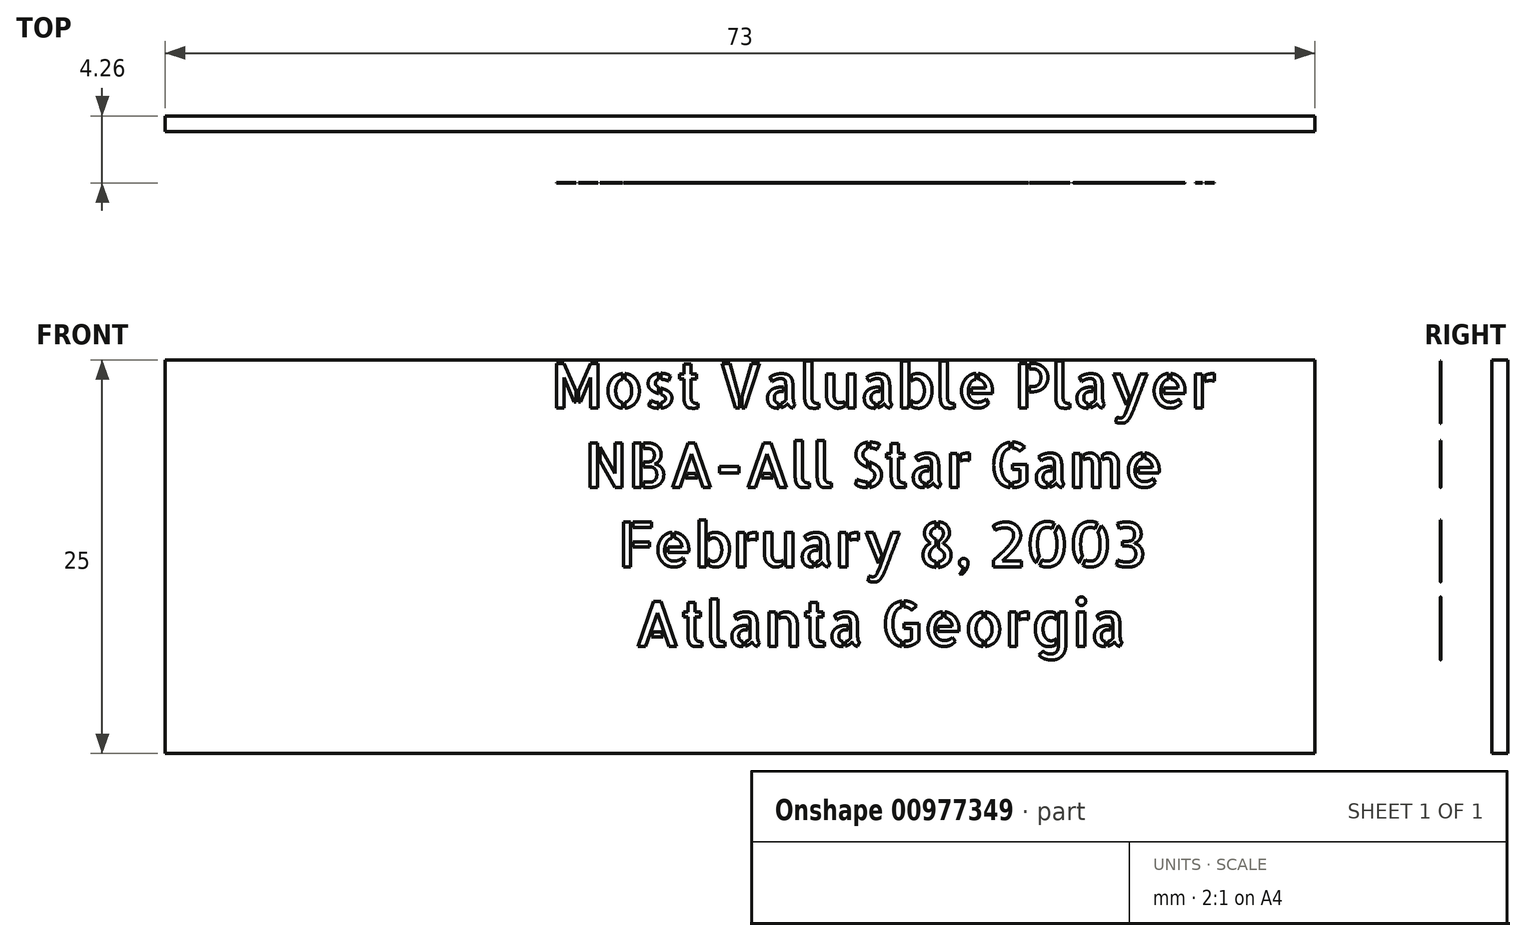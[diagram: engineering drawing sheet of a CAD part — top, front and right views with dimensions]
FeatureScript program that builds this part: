
annotation { "Feature Type Name" : "Feature", "Feature Type Description" : "" }
export const myFeature = defineFeature(function(context is Context, id is Id, definition is map)
    precondition{}
    {
        {
            var Q0;
            Q0=qCreatedBy(makeId("Front.planeOp"),FACE);
            var sketch = newSketch(context, id + "F0", { "sketchPlane" : qUnion([Q0])});
            skLineSegment(sketch, "E0.bottom", {"start": v(36.5, 12.5) * mm, "end": v(-36.5, 12.5) * mm});
            skLineSegment(sketch, "E0.top", {"start": v(36.5, -12.5) * mm, "end": v(-36.5, -12.5) * mm});
            skLineSegment(sketch, "E0.left", {"start": v(36.5, 12.5) * mm, "end": v(36.5, -12.5) * mm});
            skLineSegment(sketch, "E0.right", {"start": v(-36.5, 12.5) * mm, "end": v(-36.5, -12.5) * mm});
            skPoint(sketch, "E0.middle", {"position": v(0, 0) * mm});
            skSolve(sketch);
        }
        {
            var Q0;
            Q0 = qSketchRegion(id + "F0", true);
            extrude(context, id + "F1", {"entities" : qUnion([Q0]), "depth" : 1 * mm, "offsetDistance" : 25 * mm});
        }
        {
            var Q0;
            Q0=makeQuery(id+"F1.opExtrude","CAP_FACE",FACE,{"disambiguationData":[OSD([sQuery(id+"F0.wireOp",EDGE,"E0.bottom"),sQuery(id+"F0.wireOp",EDGE,"E0.top"),sQuery(id+"F0.wireOp",EDGE,"E0.left"),sQuery(id+"F0.wireOp",EDGE,"E0.right")])],"isStart":false});
            cPlane(context, id + "F2", {"entities" : qUnion([Q0]), "cplaneType" : CPlaneType.OFFSET, "offset" : 25 * mm, "width" : 150 * mm, "height" : 150 * mm});
        }
        {
            var Q0;
            Q0=qCreatedBy(id+"F2.planeOp",FACE);
            var sketch = newSketch(context, id + "F3", { "sketchPlane" : qUnion([Q0])});
            skText(sketch, "E1", { "text": "                       Most Valuable Player\n                         NBA-All Star Game\n                           February 8, 2003\n                            Atlanta Georgia", "fontName": "AllertaStencil-Regular.ttf"});
            const initialGuessF3  = {"E1": [-0.03462, -0.01092, 1, 0, 0.02183]};
            skSetInitialGuess(sketch, initialGuessF3);
            skSolve(sketch);
        }
        {
            var Q0;
            Q0 = qSketchRegion(id + "F3", true);
            extrude(context, id + "F4", {"entities" : qUnion([Q0]), "depth" : .1 * mm, "offsetDistance" : 25 * mm});
        }
        {
            var Q0;
            Q0=makeQuery(id+"F4.opExtrude","SWEPT_BODY",BODY,{"disambiguationData":[OSD([sQuery(id+"F3.wireOp",EDGE,"E1.sketch_text.stroke-8"),sQuery(id+"F3.wireOp",EDGE,"E1.sketch_text.stroke-9"),sQuery(id+"F3.wireOp",EDGE,"E1.sketch_text.stroke-10"),sQuery(id+"F3.wireOp",EDGE,"E1.sketch_text.stroke-11"),sQuery(id+"F3.wireOp",EDGE,"E1.sketch_text.stroke-12"),sQuery(id+"F3.wireOp",EDGE,"E1.sketch_text.stroke-13"),sQuery(id+"F3.wireOp",EDGE,"E1.sketch_text.stroke-14"),sQuery(id+"F3.wireOp",EDGE,"E1.sketch_text.stroke-15")])]});
            var Q1;
            Q1=makeQuery(id+"F4.opExtrude","SWEPT_BODY",BODY,{"disambiguationData":[OSD([sQuery(id+"F3.wireOp",EDGE,"E1.sketch_text.stroke-16"),sQuery(id+"F3.wireOp",EDGE,"E1.sketch_text.stroke-17"),sQuery(id+"F3.wireOp",EDGE,"E1.sketch_text.stroke-18"),sQuery(id+"F3.wireOp",EDGE,"E1.sketch_text.stroke-19"),sQuery(id+"F3.wireOp",EDGE,"E1.sketch_text.stroke-20"),sQuery(id+"F3.wireOp",EDGE,"E1.sketch_text.stroke-21"),sQuery(id+"F3.wireOp",EDGE,"E1.sketch_text.stroke-22"),sQuery(id+"F3.wireOp",EDGE,"E1.sketch_text.stroke-23"),sQuery(id+"F3.wireOp",EDGE,"E1.sketch_text.stroke-24"),sQuery(id+"F3.wireOp",EDGE,"E1.sketch_text.stroke-25"),sQuery(id+"F3.wireOp",EDGE,"E1.sketch_text.stroke-26"),sQuery(id+"F3.wireOp",EDGE,"E1.sketch_text.stroke-27"),sQuery(id+"F3.wireOp",EDGE,"E1.sketch_text.stroke-28"),sQuery(id+"F3.wireOp",EDGE,"E1.sketch_text.stroke-29"),sQuery(id+"F3.wireOp",EDGE,"E1.sketch_text.stroke-30"),sQuery(id+"F3.wireOp",EDGE,"E1.sketch_text.stroke-31")])]});
            var Q2;
            Q2=makeQuery(id+"F4.opExtrude","SWEPT_BODY",BODY,{"disambiguationData":[OSD([sQuery(id+"F3.wireOp",EDGE,"E1.sketch_text.stroke-32"),sQuery(id+"F3.wireOp",EDGE,"E1.sketch_text.stroke-33"),sQuery(id+"F3.wireOp",EDGE,"E1.sketch_text.stroke-34"),sQuery(id+"F3.wireOp",EDGE,"E1.sketch_text.stroke-35"),sQuery(id+"F3.wireOp",EDGE,"E1.sketch_text.stroke-36"),sQuery(id+"F3.wireOp",EDGE,"E1.sketch_text.stroke-37"),sQuery(id+"F3.wireOp",EDGE,"E1.sketch_text.stroke-38"),sQuery(id+"F3.wireOp",EDGE,"E1.sketch_text.stroke-39"),sQuery(id+"F3.wireOp",EDGE,"E1.sketch_text.stroke-40"),sQuery(id+"F3.wireOp",EDGE,"E1.sketch_text.stroke-41"),sQuery(id+"F3.wireOp",EDGE,"E1.sketch_text.stroke-42"),sQuery(id+"F3.wireOp",EDGE,"E1.sketch_text.stroke-43"),sQuery(id+"F3.wireOp",EDGE,"E1.sketch_text.stroke-44"),sQuery(id+"F3.wireOp",EDGE,"E1.sketch_text.stroke-45"),sQuery(id+"F3.wireOp",EDGE,"E1.sketch_text.stroke-46"),sQuery(id+"F3.wireOp",EDGE,"E1.sketch_text.stroke-47")])]});
            var Q3;
            Q3=makeQuery(id+"F4.opExtrude","SWEPT_BODY",BODY,{"disambiguationData":[OSD([sQuery(id+"F3.wireOp",EDGE,"E1.sketch_text.stroke-48"),sQuery(id+"F3.wireOp",EDGE,"E1.sketch_text.stroke-49"),sQuery(id+"F3.wireOp",EDGE,"E1.sketch_text.stroke-50"),sQuery(id+"F3.wireOp",EDGE,"E1.sketch_text.stroke-51"),sQuery(id+"F3.wireOp",EDGE,"E1.sketch_text.stroke-52"),sQuery(id+"F3.wireOp",EDGE,"E1.sketch_text.stroke-53"),sQuery(id+"F3.wireOp",EDGE,"E1.sketch_text.stroke-54"),sQuery(id+"F3.wireOp",EDGE,"E1.sketch_text.stroke-55"),sQuery(id+"F3.wireOp",EDGE,"E1.sketch_text.stroke-56"),sQuery(id+"F3.wireOp",EDGE,"E1.sketch_text.stroke-57"),sQuery(id+"F3.wireOp",EDGE,"E1.sketch_text.stroke-58"),sQuery(id+"F3.wireOp",EDGE,"E1.sketch_text.stroke-59"),sQuery(id+"F3.wireOp",EDGE,"E1.sketch_text.stroke-60"),sQuery(id+"F3.wireOp",EDGE,"E1.sketch_text.stroke-61")])]});
            var Q4;
            Q4=makeQuery(id+"F4.opExtrude","SWEPT_BODY",BODY,{"disambiguationData":[OSD([sQuery(id+"F3.wireOp",EDGE,"E1.sketch_text.stroke-62"),sQuery(id+"F3.wireOp",EDGE,"E1.sketch_text.stroke-63"),sQuery(id+"F3.wireOp",EDGE,"E1.sketch_text.stroke-64"),sQuery(id+"F3.wireOp",EDGE,"E1.sketch_text.stroke-65"),sQuery(id+"F3.wireOp",EDGE,"E1.sketch_text.stroke-66"),sQuery(id+"F3.wireOp",EDGE,"E1.sketch_text.stroke-67")])]});
            var Q5;
            Q5=makeQuery(id+"F4.opExtrude","SWEPT_BODY",BODY,{"disambiguationData":[OSD([sQuery(id+"F3.wireOp",EDGE,"E1.sketch_text.stroke-68"),sQuery(id+"F3.wireOp",EDGE,"E1.sketch_text.stroke-69"),sQuery(id+"F3.wireOp",EDGE,"E1.sketch_text.stroke-70"),sQuery(id+"F3.wireOp",EDGE,"E1.sketch_text.stroke-71"),sQuery(id+"F3.wireOp",EDGE,"E1.sketch_text.stroke-72"),sQuery(id+"F3.wireOp",EDGE,"E1.sketch_text.stroke-73"),sQuery(id+"F3.wireOp",EDGE,"E1.sketch_text.stroke-74"),sQuery(id+"F3.wireOp",EDGE,"E1.sketch_text.stroke-75"),sQuery(id+"F3.wireOp",EDGE,"E1.sketch_text.stroke-76")])]});
            var Q6;
            Q6=makeQuery(id+"F4.opExtrude","SWEPT_BODY",BODY,{"disambiguationData":[OSD([sQuery(id+"F3.wireOp",EDGE,"E1.sketch_text.stroke-77"),sQuery(id+"F3.wireOp",EDGE,"E1.sketch_text.stroke-78"),sQuery(id+"F3.wireOp",EDGE,"E1.sketch_text.stroke-79"),sQuery(id+"F3.wireOp",EDGE,"E1.sketch_text.stroke-80"),sQuery(id+"F3.wireOp",EDGE,"E1.sketch_text.stroke-81"),sQuery(id+"F3.wireOp",EDGE,"E1.sketch_text.stroke-82"),sQuery(id+"F3.wireOp",EDGE,"E1.sketch_text.stroke-83"),sQuery(id+"F3.wireOp",EDGE,"E1.sketch_text.stroke-84"),sQuery(id+"F3.wireOp",EDGE,"E1.sketch_text.stroke-85"),sQuery(id+"F3.wireOp",EDGE,"E1.sketch_text.stroke-86"),sQuery(id+"F3.wireOp",EDGE,"E1.sketch_text.stroke-87"),sQuery(id+"F3.wireOp",EDGE,"E1.sketch_text.stroke-88"),sQuery(id+"F3.wireOp",EDGE,"E1.sketch_text.stroke-89"),sQuery(id+"F3.wireOp",EDGE,"E1.sketch_text.stroke-90")])]});
            var Q7;
            Q7=makeQuery(id+"F4.opExtrude","SWEPT_BODY",BODY,{"disambiguationData":[OSD([sQuery(id+"F3.wireOp",EDGE,"E1.sketch_text.stroke-91"),sQuery(id+"F3.wireOp",EDGE,"E1.sketch_text.stroke-92"),sQuery(id+"F3.wireOp",EDGE,"E1.sketch_text.stroke-93"),sQuery(id+"F3.wireOp",EDGE,"E1.sketch_text.stroke-94"),sQuery(id+"F3.wireOp",EDGE,"E1.sketch_text.stroke-95"),sQuery(id+"F3.wireOp",EDGE,"E1.sketch_text.stroke-96"),sQuery(id+"F3.wireOp",EDGE,"E1.sketch_text.stroke-97"),sQuery(id+"F3.wireOp",EDGE,"E1.sketch_text.stroke-98"),sQuery(id+"F3.wireOp",EDGE,"E1.sketch_text.stroke-99"),sQuery(id+"F3.wireOp",EDGE,"E1.sketch_text.stroke-100"),sQuery(id+"F3.wireOp",EDGE,"E1.sketch_text.stroke-101"),sQuery(id+"F3.wireOp",EDGE,"E1.sketch_text.stroke-102"),sQuery(id+"F3.wireOp",EDGE,"E1.sketch_text.stroke-103"),sQuery(id+"F3.wireOp",EDGE,"E1.sketch_text.stroke-104"),sQuery(id+"F3.wireOp",EDGE,"E1.sketch_text.stroke-105"),sQuery(id+"F3.wireOp",EDGE,"E1.sketch_text.stroke-106"),sQuery(id+"F3.wireOp",EDGE,"E1.sketch_text.stroke-107"),sQuery(id+"F3.wireOp",EDGE,"E1.sketch_text.stroke-108"),sQuery(id+"F3.wireOp",EDGE,"E1.sketch_text.stroke-109"),sQuery(id+"F3.wireOp",EDGE,"E1.sketch_text.stroke-110"),sQuery(id+"F3.wireOp",EDGE,"E1.sketch_text.stroke-111"),sQuery(id+"F3.wireOp",EDGE,"E1.sketch_text.stroke-112"),sQuery(id+"F3.wireOp",EDGE,"E1.sketch_text.stroke-113"),sQuery(id+"F3.wireOp",EDGE,"E1.sketch_text.stroke-114"),sQuery(id+"F3.wireOp",EDGE,"E1.sketch_text.stroke-115")])]});
            var Q8;
            Q8=makeQuery(id+"F4.opExtrude","SWEPT_BODY",BODY,{"disambiguationData":[OSD([sQuery(id+"F3.wireOp",EDGE,"E1.sketch_text.stroke-116"),sQuery(id+"F3.wireOp",EDGE,"E1.sketch_text.stroke-117"),sQuery(id+"F3.wireOp",EDGE,"E1.sketch_text.stroke-118"),sQuery(id+"F3.wireOp",EDGE,"E1.sketch_text.stroke-119"),sQuery(id+"F3.wireOp",EDGE,"E1.sketch_text.stroke-120")])]});
            var Q9;
            Q9=makeQuery(id+"F4.opExtrude","SWEPT_BODY",BODY,{"disambiguationData":[OSD([sQuery(id+"F3.wireOp",EDGE,"E1.sketch_text.stroke-121"),sQuery(id+"F3.wireOp",EDGE,"E1.sketch_text.stroke-122"),sQuery(id+"F3.wireOp",EDGE,"E1.sketch_text.stroke-123"),sQuery(id+"F3.wireOp",EDGE,"E1.sketch_text.stroke-124"),sQuery(id+"F3.wireOp",EDGE,"E1.sketch_text.stroke-125")])]});
            var Q10;
            Q10=makeQuery(id+"F4.opExtrude","SWEPT_BODY",BODY,{"disambiguationData":[OSD([sQuery(id+"F3.wireOp",EDGE,"E1.sketch_text.stroke-126"),sQuery(id+"F3.wireOp",EDGE,"E1.sketch_text.stroke-127"),sQuery(id+"F3.wireOp",EDGE,"E1.sketch_text.stroke-128"),sQuery(id+"F3.wireOp",EDGE,"E1.sketch_text.stroke-129"),sQuery(id+"F3.wireOp",EDGE,"E1.sketch_text.stroke-130"),sQuery(id+"F3.wireOp",EDGE,"E1.sketch_text.stroke-131"),sQuery(id+"F3.wireOp",EDGE,"E1.sketch_text.stroke-132"),sQuery(id+"F3.wireOp",EDGE,"E1.sketch_text.stroke-133"),sQuery(id+"F3.wireOp",EDGE,"E1.sketch_text.stroke-134"),sQuery(id+"F3.wireOp",EDGE,"E1.sketch_text.stroke-135"),sQuery(id+"F3.wireOp",EDGE,"E1.sketch_text.stroke-136"),sQuery(id+"F3.wireOp",EDGE,"E1.sketch_text.stroke-137"),sQuery(id+"F3.wireOp",EDGE,"E1.sketch_text.stroke-138"),sQuery(id+"F3.wireOp",EDGE,"E1.sketch_text.stroke-139"),sQuery(id+"F3.wireOp",EDGE,"E1.sketch_text.stroke-140"),sQuery(id+"F3.wireOp",EDGE,"E1.sketch_text.stroke-141"),sQuery(id+"F3.wireOp",EDGE,"E1.sketch_text.stroke-142"),sQuery(id+"F3.wireOp",EDGE,"E1.sketch_text.stroke-143"),sQuery(id+"F3.wireOp",EDGE,"E1.sketch_text.stroke-144")])]});
            var Q11;
            Q11=makeQuery(id+"F4.opExtrude","SWEPT_BODY",BODY,{"disambiguationData":[OSD([sQuery(id+"F3.wireOp",EDGE,"E1.sketch_text.stroke-145"),sQuery(id+"F3.wireOp",EDGE,"E1.sketch_text.stroke-146"),sQuery(id+"F3.wireOp",EDGE,"E1.sketch_text.stroke-147"),sQuery(id+"F3.wireOp",EDGE,"E1.sketch_text.stroke-148"),sQuery(id+"F3.wireOp",EDGE,"E1.sketch_text.stroke-149"),sQuery(id+"F3.wireOp",EDGE,"E1.sketch_text.stroke-150"),sQuery(id+"F3.wireOp",EDGE,"E1.sketch_text.stroke-151"),sQuery(id+"F3.wireOp",EDGE,"E1.sketch_text.stroke-152"),sQuery(id+"F3.wireOp",EDGE,"E1.sketch_text.stroke-153"),sQuery(id+"F3.wireOp",EDGE,"E1.sketch_text.stroke-154"),sQuery(id+"F3.wireOp",EDGE,"E1.sketch_text.stroke-155"),sQuery(id+"F3.wireOp",EDGE,"E1.sketch_text.stroke-156"),sQuery(id+"F3.wireOp",EDGE,"E1.sketch_text.stroke-157"),sQuery(id+"F3.wireOp",EDGE,"E1.sketch_text.stroke-158"),sQuery(id+"F3.wireOp",EDGE,"E1.sketch_text.stroke-159"),sQuery(id+"F3.wireOp",EDGE,"E1.sketch_text.stroke-160"),sQuery(id+"F3.wireOp",EDGE,"E1.sketch_text.stroke-161"),sQuery(id+"F3.wireOp",EDGE,"E1.sketch_text.stroke-162"),sQuery(id+"F3.wireOp",EDGE,"E1.sketch_text.stroke-163"),sQuery(id+"F3.wireOp",EDGE,"E1.sketch_text.stroke-164"),sQuery(id+"F3.wireOp",EDGE,"E1.sketch_text.stroke-165"),sQuery(id+"F3.wireOp",EDGE,"E1.sketch_text.stroke-166"),sQuery(id+"F3.wireOp",EDGE,"E1.sketch_text.stroke-167"),sQuery(id+"F3.wireOp",EDGE,"E1.sketch_text.stroke-168"),sQuery(id+"F3.wireOp",EDGE,"E1.sketch_text.stroke-169"),sQuery(id+"F3.wireOp",EDGE,"E1.sketch_text.stroke-170"),sQuery(id+"F3.wireOp",EDGE,"E1.sketch_text.stroke-171"),sQuery(id+"F3.wireOp",EDGE,"E1.sketch_text.stroke-172"),sQuery(id+"F3.wireOp",EDGE,"E1.sketch_text.stroke-173"),sQuery(id+"F3.wireOp",EDGE,"E1.sketch_text.stroke-174"),sQuery(id+"F3.wireOp",EDGE,"E1.sketch_text.stroke-175"),sQuery(id+"F3.wireOp",EDGE,"E1.sketch_text.stroke-176"),sQuery(id+"F3.wireOp",EDGE,"E1.sketch_text.stroke-177"),sQuery(id+"F3.wireOp",EDGE,"E1.sketch_text.stroke-178"),sQuery(id+"F3.wireOp",EDGE,"E1.sketch_text.stroke-179"),sQuery(id+"F3.wireOp",EDGE,"E1.sketch_text.stroke-180")])]});
            var Q12;
            Q12=makeQuery(id+"F4.opExtrude","SWEPT_BODY",BODY,{"disambiguationData":[OSD([sQuery(id+"F3.wireOp",EDGE,"E1.sketch_text.stroke-181"),sQuery(id+"F3.wireOp",EDGE,"E1.sketch_text.stroke-182"),sQuery(id+"F3.wireOp",EDGE,"E1.sketch_text.stroke-183"),sQuery(id+"F3.wireOp",EDGE,"E1.sketch_text.stroke-184"),sQuery(id+"F3.wireOp",EDGE,"E1.sketch_text.stroke-185"),sQuery(id+"F3.wireOp",EDGE,"E1.sketch_text.stroke-186"),sQuery(id+"F3.wireOp",EDGE,"E1.sketch_text.stroke-187"),sQuery(id+"F3.wireOp",EDGE,"E1.sketch_text.stroke-188"),sQuery(id+"F3.wireOp",EDGE,"E1.sketch_text.stroke-189"),sQuery(id+"F3.wireOp",EDGE,"E1.sketch_text.stroke-190"),sQuery(id+"F3.wireOp",EDGE,"E1.sketch_text.stroke-191"),sQuery(id+"F3.wireOp",EDGE,"E1.sketch_text.stroke-192"),sQuery(id+"F3.wireOp",EDGE,"E1.sketch_text.stroke-193"),sQuery(id+"F3.wireOp",EDGE,"E1.sketch_text.stroke-194"),sQuery(id+"F3.wireOp",EDGE,"E1.sketch_text.stroke-195"),sQuery(id+"F3.wireOp",EDGE,"E1.sketch_text.stroke-196"),sQuery(id+"F3.wireOp",EDGE,"E1.sketch_text.stroke-197"),sQuery(id+"F3.wireOp",EDGE,"E1.sketch_text.stroke-198")])]});
            var Q13;
            Q13=makeQuery(id+"F4.opExtrude","SWEPT_BODY",BODY,{"disambiguationData":[OSD([sQuery(id+"F3.wireOp",EDGE,"E1.sketch_text.stroke-199"),sQuery(id+"F3.wireOp",EDGE,"E1.sketch_text.stroke-200"),sQuery(id+"F3.wireOp",EDGE,"E1.sketch_text.stroke-201"),sQuery(id+"F3.wireOp",EDGE,"E1.sketch_text.stroke-202"),sQuery(id+"F3.wireOp",EDGE,"E1.sketch_text.stroke-203"),sQuery(id+"F3.wireOp",EDGE,"E1.sketch_text.stroke-204"),sQuery(id+"F3.wireOp",EDGE,"E1.sketch_text.stroke-205"),sQuery(id+"F3.wireOp",EDGE,"E1.sketch_text.stroke-206"),sQuery(id+"F3.wireOp",EDGE,"E1.sketch_text.stroke-207"),sQuery(id+"F3.wireOp",EDGE,"E1.sketch_text.stroke-208"),sQuery(id+"F3.wireOp",EDGE,"E1.sketch_text.stroke-209"),sQuery(id+"F3.wireOp",EDGE,"E1.sketch_text.stroke-210"),sQuery(id+"F3.wireOp",EDGE,"E1.sketch_text.stroke-211"),sQuery(id+"F3.wireOp",EDGE,"E1.sketch_text.stroke-212"),sQuery(id+"F3.wireOp",EDGE,"E1.sketch_text.stroke-213"),sQuery(id+"F3.wireOp",EDGE,"E1.sketch_text.stroke-214"),sQuery(id+"F3.wireOp",EDGE,"E1.sketch_text.stroke-215"),sQuery(id+"F3.wireOp",EDGE,"E1.sketch_text.stroke-216"),sQuery(id+"F3.wireOp",EDGE,"E1.sketch_text.stroke-217"),sQuery(id+"F3.wireOp",EDGE,"E1.sketch_text.stroke-218")])]});
            var Q14;
            Q14=makeQuery(id+"F4.opExtrude","SWEPT_BODY",BODY,{"disambiguationData":[OSD([sQuery(id+"F3.wireOp",EDGE,"E1.sketch_text.stroke-219"),sQuery(id+"F3.wireOp",EDGE,"E1.sketch_text.stroke-220"),sQuery(id+"F3.wireOp",EDGE,"E1.sketch_text.stroke-221"),sQuery(id+"F3.wireOp",EDGE,"E1.sketch_text.stroke-222"),sQuery(id+"F3.wireOp",EDGE,"E1.sketch_text.stroke-223")])]});
            var Q15;
            Q15=makeQuery(id+"F4.opExtrude","SWEPT_BODY",BODY,{"disambiguationData":[OSD([sQuery(id+"F3.wireOp",EDGE,"E1.sketch_text.stroke-224"),sQuery(id+"F3.wireOp",EDGE,"E1.sketch_text.stroke-225"),sQuery(id+"F3.wireOp",EDGE,"E1.sketch_text.stroke-226"),sQuery(id+"F3.wireOp",EDGE,"E1.sketch_text.stroke-227"),sQuery(id+"F3.wireOp",EDGE,"E1.sketch_text.stroke-228"),sQuery(id+"F3.wireOp",EDGE,"E1.sketch_text.stroke-229"),sQuery(id+"F3.wireOp",EDGE,"E1.sketch_text.stroke-230"),sQuery(id+"F3.wireOp",EDGE,"E1.sketch_text.stroke-231"),sQuery(id+"F3.wireOp",EDGE,"E1.sketch_text.stroke-232"),sQuery(id+"F3.wireOp",EDGE,"E1.sketch_text.stroke-233"),sQuery(id+"F3.wireOp",EDGE,"E1.sketch_text.stroke-234"),sQuery(id+"F3.wireOp",EDGE,"E1.sketch_text.stroke-235"),sQuery(id+"F3.wireOp",EDGE,"E1.sketch_text.stroke-236"),sQuery(id+"F3.wireOp",EDGE,"E1.sketch_text.stroke-237"),sQuery(id+"F3.wireOp",EDGE,"E1.sketch_text.stroke-238"),sQuery(id+"F3.wireOp",EDGE,"E1.sketch_text.stroke-239"),sQuery(id+"F3.wireOp",EDGE,"E1.sketch_text.stroke-240"),sQuery(id+"F3.wireOp",EDGE,"E1.sketch_text.stroke-241"),sQuery(id+"F3.wireOp",EDGE,"E1.sketch_text.stroke-242")])]});
            var Q16;
            Q16=makeQuery(id+"F4.opExtrude","SWEPT_BODY",BODY,{"disambiguationData":[OSD([sQuery(id+"F3.wireOp",EDGE,"E1.sketch_text.stroke-243"),sQuery(id+"F3.wireOp",EDGE,"E1.sketch_text.stroke-244"),sQuery(id+"F3.wireOp",EDGE,"E1.sketch_text.stroke-245"),sQuery(id+"F3.wireOp",EDGE,"E1.sketch_text.stroke-246"),sQuery(id+"F3.wireOp",EDGE,"E1.sketch_text.stroke-247"),sQuery(id+"F3.wireOp",EDGE,"E1.sketch_text.stroke-248"),sQuery(id+"F3.wireOp",EDGE,"E1.sketch_text.stroke-249"),sQuery(id+"F3.wireOp",EDGE,"E1.sketch_text.stroke-250"),sQuery(id+"F3.wireOp",EDGE,"E1.sketch_text.stroke-251"),sQuery(id+"F3.wireOp",EDGE,"E1.sketch_text.stroke-252"),sQuery(id+"F3.wireOp",EDGE,"E1.sketch_text.stroke-253"),sQuery(id+"F3.wireOp",EDGE,"E1.sketch_text.stroke-254"),sQuery(id+"F3.wireOp",EDGE,"E1.sketch_text.stroke-255"),sQuery(id+"F3.wireOp",EDGE,"E1.sketch_text.stroke-256"),sQuery(id+"F3.wireOp",EDGE,"E1.sketch_text.stroke-257"),sQuery(id+"F3.wireOp",EDGE,"E1.sketch_text.stroke-258"),sQuery(id+"F3.wireOp",EDGE,"E1.sketch_text.stroke-259"),sQuery(id+"F3.wireOp",EDGE,"E1.sketch_text.stroke-260"),sQuery(id+"F3.wireOp",EDGE,"E1.sketch_text.stroke-261"),sQuery(id+"F3.wireOp",EDGE,"E1.sketch_text.stroke-262"),sQuery(id+"F3.wireOp",EDGE,"E1.sketch_text.stroke-263"),sQuery(id+"F3.wireOp",EDGE,"E1.sketch_text.stroke-264"),sQuery(id+"F3.wireOp",EDGE,"E1.sketch_text.stroke-265"),sQuery(id+"F3.wireOp",EDGE,"E1.sketch_text.stroke-266"),sQuery(id+"F3.wireOp",EDGE,"E1.sketch_text.stroke-267"),sQuery(id+"F3.wireOp",EDGE,"E1.sketch_text.stroke-268"),sQuery(id+"F3.wireOp",EDGE,"E1.sketch_text.stroke-269"),sQuery(id+"F3.wireOp",EDGE,"E1.sketch_text.stroke-270"),sQuery(id+"F3.wireOp",EDGE,"E1.sketch_text.stroke-271"),sQuery(id+"F3.wireOp",EDGE,"E1.sketch_text.stroke-272"),sQuery(id+"F3.wireOp",EDGE,"E1.sketch_text.stroke-273"),sQuery(id+"F3.wireOp",EDGE,"E1.sketch_text.stroke-274"),sQuery(id+"F3.wireOp",EDGE,"E1.sketch_text.stroke-275"),sQuery(id+"F3.wireOp",EDGE,"E1.sketch_text.stroke-276"),sQuery(id+"F3.wireOp",EDGE,"E1.sketch_text.stroke-277"),sQuery(id+"F3.wireOp",EDGE,"E1.sketch_text.stroke-278")])]});
            var Q17;
            Q17=makeQuery(id+"F4.opExtrude","SWEPT_BODY",BODY,{"disambiguationData":[OSD([sQuery(id+"F3.wireOp",EDGE,"E1.sketch_text.stroke-279"),sQuery(id+"F3.wireOp",EDGE,"E1.sketch_text.stroke-280"),sQuery(id+"F3.wireOp",EDGE,"E1.sketch_text.stroke-281"),sQuery(id+"F3.wireOp",EDGE,"E1.sketch_text.stroke-282"),sQuery(id+"F3.wireOp",EDGE,"E1.sketch_text.stroke-283"),sQuery(id+"F3.wireOp",EDGE,"E1.sketch_text.stroke-284")])]});
            var Q18;
            Q18=makeQuery(id+"F4.opExtrude","SWEPT_BODY",BODY,{"disambiguationData":[OSD([sQuery(id+"F3.wireOp",EDGE,"E1.sketch_text.stroke-285"),sQuery(id+"F3.wireOp",EDGE,"E1.sketch_text.stroke-286"),sQuery(id+"F3.wireOp",EDGE,"E1.sketch_text.stroke-287"),sQuery(id+"F3.wireOp",EDGE,"E1.sketch_text.stroke-288"),sQuery(id+"F3.wireOp",EDGE,"E1.sketch_text.stroke-289"),sQuery(id+"F3.wireOp",EDGE,"E1.sketch_text.stroke-290"),sQuery(id+"F3.wireOp",EDGE,"E1.sketch_text.stroke-291"),sQuery(id+"F3.wireOp",EDGE,"E1.sketch_text.stroke-292"),sQuery(id+"F3.wireOp",EDGE,"E1.sketch_text.stroke-293"),sQuery(id+"F3.wireOp",EDGE,"E1.sketch_text.stroke-294"),sQuery(id+"F3.wireOp",EDGE,"E1.sketch_text.stroke-295"),sQuery(id+"F3.wireOp",EDGE,"E1.sketch_text.stroke-296"),sQuery(id+"F3.wireOp",EDGE,"E1.sketch_text.stroke-297"),sQuery(id+"F3.wireOp",EDGE,"E1.sketch_text.stroke-298"),sQuery(id+"F3.wireOp",EDGE,"E1.sketch_text.stroke-299"),sQuery(id+"F3.wireOp",EDGE,"E1.sketch_text.stroke-300"),sQuery(id+"F3.wireOp",EDGE,"E1.sketch_text.stroke-301"),sQuery(id+"F3.wireOp",EDGE,"E1.sketch_text.stroke-302"),sQuery(id+"F3.wireOp",EDGE,"E1.sketch_text.stroke-303"),sQuery(id+"F3.wireOp",EDGE,"E1.sketch_text.stroke-304"),sQuery(id+"F3.wireOp",EDGE,"E1.sketch_text.stroke-305"),sQuery(id+"F3.wireOp",EDGE,"E1.sketch_text.stroke-306"),sQuery(id+"F3.wireOp",EDGE,"E1.sketch_text.stroke-307"),sQuery(id+"F3.wireOp",EDGE,"E1.sketch_text.stroke-308"),sQuery(id+"F3.wireOp",EDGE,"E1.sketch_text.stroke-309"),sQuery(id+"F3.wireOp",EDGE,"E1.sketch_text.stroke-310"),sQuery(id+"F3.wireOp",EDGE,"E1.sketch_text.stroke-311")])]});
            var Q19;
            Q19=makeQuery(id+"F4.opExtrude","SWEPT_BODY",BODY,{"disambiguationData":[OSD([sQuery(id+"F3.wireOp",EDGE,"E1.sketch_text.stroke-312"),sQuery(id+"F3.wireOp",EDGE,"E1.sketch_text.stroke-313"),sQuery(id+"F3.wireOp",EDGE,"E1.sketch_text.stroke-314"),sQuery(id+"F3.wireOp",EDGE,"E1.sketch_text.stroke-315"),sQuery(id+"F3.wireOp",EDGE,"E1.sketch_text.stroke-316"),sQuery(id+"F3.wireOp",EDGE,"E1.sketch_text.stroke-317"),sQuery(id+"F3.wireOp",EDGE,"E1.sketch_text.stroke-318"),sQuery(id+"F3.wireOp",EDGE,"E1.sketch_text.stroke-319"),sQuery(id+"F3.wireOp",EDGE,"E1.sketch_text.stroke-320"),sQuery(id+"F3.wireOp",EDGE,"E1.sketch_text.stroke-321"),sQuery(id+"F3.wireOp",EDGE,"E1.sketch_text.stroke-322"),sQuery(id+"F3.wireOp",EDGE,"E1.sketch_text.stroke-323"),sQuery(id+"F3.wireOp",EDGE,"E1.sketch_text.stroke-324"),sQuery(id+"F3.wireOp",EDGE,"E1.sketch_text.stroke-325"),sQuery(id+"F3.wireOp",EDGE,"E1.sketch_text.stroke-326"),sQuery(id+"F3.wireOp",EDGE,"E1.sketch_text.stroke-327"),sQuery(id+"F3.wireOp",EDGE,"E1.sketch_text.stroke-328"),sQuery(id+"F3.wireOp",EDGE,"E1.sketch_text.stroke-329")])]});
            var Q20;
            Q20=makeQuery(id+"F4.opExtrude","SWEPT_BODY",BODY,{"disambiguationData":[OSD([sQuery(id+"F3.wireOp",EDGE,"E1.sketch_text.stroke-330"),sQuery(id+"F3.wireOp",EDGE,"E1.sketch_text.stroke-331"),sQuery(id+"F3.wireOp",EDGE,"E1.sketch_text.stroke-332"),sQuery(id+"F3.wireOp",EDGE,"E1.sketch_text.stroke-333"),sQuery(id+"F3.wireOp",EDGE,"E1.sketch_text.stroke-334"),sQuery(id+"F3.wireOp",EDGE,"E1.sketch_text.stroke-335"),sQuery(id+"F3.wireOp",EDGE,"E1.sketch_text.stroke-336"),sQuery(id+"F3.wireOp",EDGE,"E1.sketch_text.stroke-337"),sQuery(id+"F3.wireOp",EDGE,"E1.sketch_text.stroke-338"),sQuery(id+"F3.wireOp",EDGE,"E1.sketch_text.stroke-339"),sQuery(id+"F3.wireOp",EDGE,"E1.sketch_text.stroke-340"),sQuery(id+"F3.wireOp",EDGE,"E1.sketch_text.stroke-341"),sQuery(id+"F3.wireOp",EDGE,"E1.sketch_text.stroke-342")])]});
            var Q21;
            Q21=makeQuery(id+"F4.opExtrude","SWEPT_BODY",BODY,{"disambiguationData":[OSD([sQuery(id+"F3.wireOp",EDGE,"E1.sketch_text.stroke-343"),sQuery(id+"F3.wireOp",EDGE,"E1.sketch_text.stroke-344"),sQuery(id+"F3.wireOp",EDGE,"E1.sketch_text.stroke-345"),sQuery(id+"F3.wireOp",EDGE,"E1.sketch_text.stroke-346"),sQuery(id+"F3.wireOp",EDGE,"E1.sketch_text.stroke-347"),sQuery(id+"F3.wireOp",EDGE,"E1.sketch_text.stroke-348"),sQuery(id+"F3.wireOp",EDGE,"E1.sketch_text.stroke-349"),sQuery(id+"F3.wireOp",EDGE,"E1.sketch_text.stroke-350"),sQuery(id+"F3.wireOp",EDGE,"E1.sketch_text.stroke-351"),sQuery(id+"F3.wireOp",EDGE,"E1.sketch_text.stroke-352"),sQuery(id+"F3.wireOp",EDGE,"E1.sketch_text.stroke-353"),sQuery(id+"F3.wireOp",EDGE,"E1.sketch_text.stroke-354"),sQuery(id+"F3.wireOp",EDGE,"E1.sketch_text.stroke-355"),sQuery(id+"F3.wireOp",EDGE,"E1.sketch_text.stroke-356"),sQuery(id+"F3.wireOp",EDGE,"E1.sketch_text.stroke-357"),sQuery(id+"F3.wireOp",EDGE,"E1.sketch_text.stroke-358"),sQuery(id+"F3.wireOp",EDGE,"E1.sketch_text.stroke-359"),sQuery(id+"F3.wireOp",EDGE,"E1.sketch_text.stroke-360"),sQuery(id+"F3.wireOp",EDGE,"E1.sketch_text.stroke-361"),sQuery(id+"F3.wireOp",EDGE,"E1.sketch_text.stroke-362"),sQuery(id+"F3.wireOp",EDGE,"E1.sketch_text.stroke-363"),sQuery(id+"F3.wireOp",EDGE,"E1.sketch_text.stroke-364"),sQuery(id+"F3.wireOp",EDGE,"E1.sketch_text.stroke-365"),sQuery(id+"F3.wireOp",EDGE,"E1.sketch_text.stroke-366")])]});
            var Q22;
            Q22=makeQuery(id+"F4.opExtrude","SWEPT_BODY",BODY,{"disambiguationData":[OSD([sQuery(id+"F3.wireOp",EDGE,"E1.sketch_text.stroke-367"),sQuery(id+"F3.wireOp",EDGE,"E1.sketch_text.stroke-368"),sQuery(id+"F3.wireOp",EDGE,"E1.sketch_text.stroke-369"),sQuery(id+"F3.wireOp",EDGE,"E1.sketch_text.stroke-370")])]});
            var Q23;
            Q23=makeQuery(id+"F4.opExtrude","SWEPT_BODY",BODY,{"disambiguationData":[OSD([sQuery(id+"F3.wireOp",EDGE,"E1.sketch_text.stroke-371"),sQuery(id+"F3.wireOp",EDGE,"E1.sketch_text.stroke-372"),sQuery(id+"F3.wireOp",EDGE,"E1.sketch_text.stroke-373"),sQuery(id+"F3.wireOp",EDGE,"E1.sketch_text.stroke-374"),sQuery(id+"F3.wireOp",EDGE,"E1.sketch_text.stroke-375"),sQuery(id+"F3.wireOp",EDGE,"E1.sketch_text.stroke-376"),sQuery(id+"F3.wireOp",EDGE,"E1.sketch_text.stroke-377"),sQuery(id+"F3.wireOp",EDGE,"E1.sketch_text.stroke-378"),sQuery(id+"F3.wireOp",EDGE,"E1.sketch_text.stroke-379"),sQuery(id+"F3.wireOp",EDGE,"E1.sketch_text.stroke-380"),sQuery(id+"F3.wireOp",EDGE,"E1.sketch_text.stroke-381"),sQuery(id+"F3.wireOp",EDGE,"E1.sketch_text.stroke-382"),sQuery(id+"F3.wireOp",EDGE,"E1.sketch_text.stroke-383"),sQuery(id+"F3.wireOp",EDGE,"E1.sketch_text.stroke-384"),sQuery(id+"F3.wireOp",EDGE,"E1.sketch_text.stroke-385"),sQuery(id+"F3.wireOp",EDGE,"E1.sketch_text.stroke-386"),sQuery(id+"F3.wireOp",EDGE,"E1.sketch_text.stroke-387"),sQuery(id+"F3.wireOp",EDGE,"E1.sketch_text.stroke-388"),sQuery(id+"F3.wireOp",EDGE,"E1.sketch_text.stroke-389"),sQuery(id+"F3.wireOp",EDGE,"E1.sketch_text.stroke-390"),sQuery(id+"F3.wireOp",EDGE,"E1.sketch_text.stroke-391"),sQuery(id+"F3.wireOp",EDGE,"E1.sketch_text.stroke-392")])]});
            var Q24;
            Q24=makeQuery(id+"F4.opExtrude","SWEPT_BODY",BODY,{"disambiguationData":[OSD([sQuery(id+"F3.wireOp",EDGE,"E1.sketch_text.stroke-393"),sQuery(id+"F3.wireOp",EDGE,"E1.sketch_text.stroke-394"),sQuery(id+"F3.wireOp",EDGE,"E1.sketch_text.stroke-395"),sQuery(id+"F3.wireOp",EDGE,"E1.sketch_text.stroke-396"),sQuery(id+"F3.wireOp",EDGE,"E1.sketch_text.stroke-397"),sQuery(id+"F3.wireOp",EDGE,"E1.sketch_text.stroke-398"),sQuery(id+"F3.wireOp",EDGE,"E1.sketch_text.stroke-399"),sQuery(id+"F3.wireOp",EDGE,"E1.sketch_text.stroke-400"),sQuery(id+"F3.wireOp",EDGE,"E1.sketch_text.stroke-401"),sQuery(id+"F3.wireOp",EDGE,"E1.sketch_text.stroke-402"),sQuery(id+"F3.wireOp",EDGE,"E1.sketch_text.stroke-403"),sQuery(id+"F3.wireOp",EDGE,"E1.sketch_text.stroke-404"),sQuery(id+"F3.wireOp",EDGE,"E1.sketch_text.stroke-405"),sQuery(id+"F3.wireOp",EDGE,"E1.sketch_text.stroke-406"),sQuery(id+"F3.wireOp",EDGE,"E1.sketch_text.stroke-407"),sQuery(id+"F3.wireOp",EDGE,"E1.sketch_text.stroke-408"),sQuery(id+"F3.wireOp",EDGE,"E1.sketch_text.stroke-409"),sQuery(id+"F3.wireOp",EDGE,"E1.sketch_text.stroke-410")])]});
            var Q25;
            Q25=makeQuery(id+"F4.opExtrude","SWEPT_BODY",BODY,{"disambiguationData":[OSD([sQuery(id+"F3.wireOp",EDGE,"E1.sketch_text.stroke-411"),sQuery(id+"F3.wireOp",EDGE,"E1.sketch_text.stroke-412"),sQuery(id+"F3.wireOp",EDGE,"E1.sketch_text.stroke-413"),sQuery(id+"F3.wireOp",EDGE,"E1.sketch_text.stroke-414"),sQuery(id+"F3.wireOp",EDGE,"E1.sketch_text.stroke-415"),sQuery(id+"F3.wireOp",EDGE,"E1.sketch_text.stroke-416"),sQuery(id+"F3.wireOp",EDGE,"E1.sketch_text.stroke-417"),sQuery(id+"F3.wireOp",EDGE,"E1.sketch_text.stroke-418"),sQuery(id+"F3.wireOp",EDGE,"E1.sketch_text.stroke-419"),sQuery(id+"F3.wireOp",EDGE,"E1.sketch_text.stroke-420"),sQuery(id+"F3.wireOp",EDGE,"E1.sketch_text.stroke-421"),sQuery(id+"F3.wireOp",EDGE,"E1.sketch_text.stroke-422"),sQuery(id+"F3.wireOp",EDGE,"E1.sketch_text.stroke-423"),sQuery(id+"F3.wireOp",EDGE,"E1.sketch_text.stroke-424"),sQuery(id+"F3.wireOp",EDGE,"E1.sketch_text.stroke-425"),sQuery(id+"F3.wireOp",EDGE,"E1.sketch_text.stroke-426"),sQuery(id+"F3.wireOp",EDGE,"E1.sketch_text.stroke-427"),sQuery(id+"F3.wireOp",EDGE,"E1.sketch_text.stroke-428"),sQuery(id+"F3.wireOp",EDGE,"E1.sketch_text.stroke-429")])]});
            var Q26;
            Q26=makeQuery(id+"F4.opExtrude","SWEPT_BODY",BODY,{"disambiguationData":[OSD([sQuery(id+"F3.wireOp",EDGE,"E1.sketch_text.stroke-430"),sQuery(id+"F3.wireOp",EDGE,"E1.sketch_text.stroke-431"),sQuery(id+"F3.wireOp",EDGE,"E1.sketch_text.stroke-432"),sQuery(id+"F3.wireOp",EDGE,"E1.sketch_text.stroke-433"),sQuery(id+"F3.wireOp",EDGE,"E1.sketch_text.stroke-434"),sQuery(id+"F3.wireOp",EDGE,"E1.sketch_text.stroke-435"),sQuery(id+"F3.wireOp",EDGE,"E1.sketch_text.stroke-436"),sQuery(id+"F3.wireOp",EDGE,"E1.sketch_text.stroke-437"),sQuery(id+"F3.wireOp",EDGE,"E1.sketch_text.stroke-438"),sQuery(id+"F3.wireOp",EDGE,"E1.sketch_text.stroke-439"),sQuery(id+"F3.wireOp",EDGE,"E1.sketch_text.stroke-440"),sQuery(id+"F3.wireOp",EDGE,"E1.sketch_text.stroke-441"),sQuery(id+"F3.wireOp",EDGE,"E1.sketch_text.stroke-442"),sQuery(id+"F3.wireOp",EDGE,"E1.sketch_text.stroke-443"),sQuery(id+"F3.wireOp",EDGE,"E1.sketch_text.stroke-444"),sQuery(id+"F3.wireOp",EDGE,"E1.sketch_text.stroke-445"),sQuery(id+"F3.wireOp",EDGE,"E1.sketch_text.stroke-446"),sQuery(id+"F3.wireOp",EDGE,"E1.sketch_text.stroke-447"),sQuery(id+"F3.wireOp",EDGE,"E1.sketch_text.stroke-448"),sQuery(id+"F3.wireOp",EDGE,"E1.sketch_text.stroke-449"),sQuery(id+"F3.wireOp",EDGE,"E1.sketch_text.stroke-450"),sQuery(id+"F3.wireOp",EDGE,"E1.sketch_text.stroke-451"),sQuery(id+"F3.wireOp",EDGE,"E1.sketch_text.stroke-452"),sQuery(id+"F3.wireOp",EDGE,"E1.sketch_text.stroke-453"),sQuery(id+"F3.wireOp",EDGE,"E1.sketch_text.stroke-454"),sQuery(id+"F3.wireOp",EDGE,"E1.sketch_text.stroke-455"),sQuery(id+"F3.wireOp",EDGE,"E1.sketch_text.stroke-456"),sQuery(id+"F3.wireOp",EDGE,"E1.sketch_text.stroke-457"),sQuery(id+"F3.wireOp",EDGE,"E1.sketch_text.stroke-458"),sQuery(id+"F3.wireOp",EDGE,"E1.sketch_text.stroke-459"),sQuery(id+"F3.wireOp",EDGE,"E1.sketch_text.stroke-460"),sQuery(id+"F3.wireOp",EDGE,"E1.sketch_text.stroke-461"),sQuery(id+"F3.wireOp",EDGE,"E1.sketch_text.stroke-462"),sQuery(id+"F3.wireOp",EDGE,"E1.sketch_text.stroke-463"),sQuery(id+"F3.wireOp",EDGE,"E1.sketch_text.stroke-464"),sQuery(id+"F3.wireOp",EDGE,"E1.sketch_text.stroke-465")])]});
            var Q27;
            Q27=makeQuery(id+"F4.opExtrude","SWEPT_BODY",BODY,{"disambiguationData":[OSD([sQuery(id+"F3.wireOp",EDGE,"E1.sketch_text.stroke-466"),sQuery(id+"F3.wireOp",EDGE,"E1.sketch_text.stroke-467"),sQuery(id+"F3.wireOp",EDGE,"E1.sketch_text.stroke-468"),sQuery(id+"F3.wireOp",EDGE,"E1.sketch_text.stroke-469"),sQuery(id+"F3.wireOp",EDGE,"E1.sketch_text.stroke-470"),sQuery(id+"F3.wireOp",EDGE,"E1.sketch_text.stroke-471"),sQuery(id+"F3.wireOp",EDGE,"E1.sketch_text.stroke-472"),sQuery(id+"F3.wireOp",EDGE,"E1.sketch_text.stroke-473"),sQuery(id+"F3.wireOp",EDGE,"E1.sketch_text.stroke-474"),sQuery(id+"F3.wireOp",EDGE,"E1.sketch_text.stroke-475"),sQuery(id+"F3.wireOp",EDGE,"E1.sketch_text.stroke-476"),sQuery(id+"F3.wireOp",EDGE,"E1.sketch_text.stroke-477"),sQuery(id+"F3.wireOp",EDGE,"E1.sketch_text.stroke-478"),sQuery(id+"F3.wireOp",EDGE,"E1.sketch_text.stroke-479"),sQuery(id+"F3.wireOp",EDGE,"E1.sketch_text.stroke-480"),sQuery(id+"F3.wireOp",EDGE,"E1.sketch_text.stroke-481"),sQuery(id+"F3.wireOp",EDGE,"E1.sketch_text.stroke-482"),sQuery(id+"F3.wireOp",EDGE,"E1.sketch_text.stroke-483"),sQuery(id+"F3.wireOp",EDGE,"E1.sketch_text.stroke-484"),sQuery(id+"F3.wireOp",EDGE,"E1.sketch_text.stroke-485"),sQuery(id+"F3.wireOp",EDGE,"E1.sketch_text.stroke-486"),sQuery(id+"F3.wireOp",EDGE,"E1.sketch_text.stroke-487"),sQuery(id+"F3.wireOp",EDGE,"E1.sketch_text.stroke-488"),sQuery(id+"F3.wireOp",EDGE,"E1.sketch_text.stroke-489")])]});
            var Q28;
            Q28=makeQuery(id+"F4.opExtrude","SWEPT_BODY",BODY,{"disambiguationData":[OSD([sQuery(id+"F3.wireOp",EDGE,"E1.sketch_text.stroke-490"),sQuery(id+"F3.wireOp",EDGE,"E1.sketch_text.stroke-491"),sQuery(id+"F3.wireOp",EDGE,"E1.sketch_text.stroke-492"),sQuery(id+"F3.wireOp",EDGE,"E1.sketch_text.stroke-493"),sQuery(id+"F3.wireOp",EDGE,"E1.sketch_text.stroke-494")])]});
            var Q29;
            Q29=makeQuery(id+"F4.opExtrude","SWEPT_BODY",BODY,{"disambiguationData":[OSD([sQuery(id+"F3.wireOp",EDGE,"E1.sketch_text.stroke-495"),sQuery(id+"F3.wireOp",EDGE,"E1.sketch_text.stroke-496"),sQuery(id+"F3.wireOp",EDGE,"E1.sketch_text.stroke-497"),sQuery(id+"F3.wireOp",EDGE,"E1.sketch_text.stroke-498"),sQuery(id+"F3.wireOp",EDGE,"E1.sketch_text.stroke-499"),sQuery(id+"F3.wireOp",EDGE,"E1.sketch_text.stroke-500"),sQuery(id+"F3.wireOp",EDGE,"E1.sketch_text.stroke-501"),sQuery(id+"F3.wireOp",EDGE,"E1.sketch_text.stroke-502"),sQuery(id+"F3.wireOp",EDGE,"E1.sketch_text.stroke-503"),sQuery(id+"F3.wireOp",EDGE,"E1.sketch_text.stroke-504"),sQuery(id+"F3.wireOp",EDGE,"E1.sketch_text.stroke-505"),sQuery(id+"F3.wireOp",EDGE,"E1.sketch_text.stroke-506"),sQuery(id+"F3.wireOp",EDGE,"E1.sketch_text.stroke-507")])]});
            var Q30;
            Q30=makeQuery(id+"F4.opExtrude","SWEPT_BODY",BODY,{"disambiguationData":[OSD([sQuery(id+"F3.wireOp",EDGE,"E1.sketch_text.stroke-508"),sQuery(id+"F3.wireOp",EDGE,"E1.sketch_text.stroke-509"),sQuery(id+"F3.wireOp",EDGE,"E1.sketch_text.stroke-510"),sQuery(id+"F3.wireOp",EDGE,"E1.sketch_text.stroke-511"),sQuery(id+"F3.wireOp",EDGE,"E1.sketch_text.stroke-512"),sQuery(id+"F3.wireOp",EDGE,"E1.sketch_text.stroke-513"),sQuery(id+"F3.wireOp",EDGE,"E1.sketch_text.stroke-514"),sQuery(id+"F3.wireOp",EDGE,"E1.sketch_text.stroke-515"),sQuery(id+"F3.wireOp",EDGE,"E1.sketch_text.stroke-516"),sQuery(id+"F3.wireOp",EDGE,"E1.sketch_text.stroke-517"),sQuery(id+"F3.wireOp",EDGE,"E1.sketch_text.stroke-518"),sQuery(id+"F3.wireOp",EDGE,"E1.sketch_text.stroke-519"),sQuery(id+"F3.wireOp",EDGE,"E1.sketch_text.stroke-520"),sQuery(id+"F3.wireOp",EDGE,"E1.sketch_text.stroke-521"),sQuery(id+"F3.wireOp",EDGE,"E1.sketch_text.stroke-522"),sQuery(id+"F3.wireOp",EDGE,"E1.sketch_text.stroke-523"),sQuery(id+"F3.wireOp",EDGE,"E1.sketch_text.stroke-524"),sQuery(id+"F3.wireOp",EDGE,"E1.sketch_text.stroke-525"),sQuery(id+"F3.wireOp",EDGE,"E1.sketch_text.stroke-526"),sQuery(id+"F3.wireOp",EDGE,"E1.sketch_text.stroke-527"),sQuery(id+"F3.wireOp",EDGE,"E1.sketch_text.stroke-528"),sQuery(id+"F3.wireOp",EDGE,"E1.sketch_text.stroke-529"),sQuery(id+"F3.wireOp",EDGE,"E1.sketch_text.stroke-530"),sQuery(id+"F3.wireOp",EDGE,"E1.sketch_text.stroke-531")])]});
            var Q31;
            Q31=makeQuery(id+"F4.opExtrude","SWEPT_BODY",BODY,{"disambiguationData":[OSD([sQuery(id+"F3.wireOp",EDGE,"E1.sketch_text.stroke-532"),sQuery(id+"F3.wireOp",EDGE,"E1.sketch_text.stroke-533"),sQuery(id+"F3.wireOp",EDGE,"E1.sketch_text.stroke-534"),sQuery(id+"F3.wireOp",EDGE,"E1.sketch_text.stroke-535"),sQuery(id+"F3.wireOp",EDGE,"E1.sketch_text.stroke-536"),sQuery(id+"F3.wireOp",EDGE,"E1.sketch_text.stroke-537"),sQuery(id+"F3.wireOp",EDGE,"E1.sketch_text.stroke-538")])]});
            var Q32;
            Q32=makeQuery(id+"F4.opExtrude","SWEPT_BODY",BODY,{"disambiguationData":[OSD([sQuery(id+"F3.wireOp",EDGE,"E1.sketch_text.stroke-539"),sQuery(id+"F3.wireOp",EDGE,"E1.sketch_text.stroke-540"),sQuery(id+"F3.wireOp",EDGE,"E1.sketch_text.stroke-541"),sQuery(id+"F3.wireOp",EDGE,"E1.sketch_text.stroke-542"),sQuery(id+"F3.wireOp",EDGE,"E1.sketch_text.stroke-543"),sQuery(id+"F3.wireOp",EDGE,"E1.sketch_text.stroke-544"),sQuery(id+"F3.wireOp",EDGE,"E1.sketch_text.stroke-545")])]});
            var Q33;
            Q33=makeQuery(id+"F4.opExtrude","SWEPT_BODY",BODY,{"disambiguationData":[OSD([sQuery(id+"F3.wireOp",EDGE,"E1.sketch_text.stroke-546"),sQuery(id+"F3.wireOp",EDGE,"E1.sketch_text.stroke-547"),sQuery(id+"F3.wireOp",EDGE,"E1.sketch_text.stroke-548"),sQuery(id+"F3.wireOp",EDGE,"E1.sketch_text.stroke-549"),sQuery(id+"F3.wireOp",EDGE,"E1.sketch_text.stroke-550"),sQuery(id+"F3.wireOp",EDGE,"E1.sketch_text.stroke-551"),sQuery(id+"F3.wireOp",EDGE,"E1.sketch_text.stroke-552")])]});
            var Q34;
            Q34=makeQuery(id+"F4.opExtrude","SWEPT_BODY",BODY,{"disambiguationData":[OSD([sQuery(id+"F3.wireOp",EDGE,"E1.sketch_text.stroke-553"),sQuery(id+"F3.wireOp",EDGE,"E1.sketch_text.stroke-554"),sQuery(id+"F3.wireOp",EDGE,"E1.sketch_text.stroke-555"),sQuery(id+"F3.wireOp",EDGE,"E1.sketch_text.stroke-556")])]});
            var Q35;
            Q35=makeQuery(id+"F4.opExtrude","SWEPT_BODY",BODY,{"disambiguationData":[OSD([sQuery(id+"F3.wireOp",EDGE,"E1.sketch_text.stroke-557"),sQuery(id+"F3.wireOp",EDGE,"E1.sketch_text.stroke-558"),sQuery(id+"F3.wireOp",EDGE,"E1.sketch_text.stroke-559"),sQuery(id+"F3.wireOp",EDGE,"E1.sketch_text.stroke-560"),sQuery(id+"F3.wireOp",EDGE,"E1.sketch_text.stroke-561"),sQuery(id+"F3.wireOp",EDGE,"E1.sketch_text.stroke-562"),sQuery(id+"F3.wireOp",EDGE,"E1.sketch_text.stroke-563"),sQuery(id+"F3.wireOp",EDGE,"E1.sketch_text.stroke-564"),sQuery(id+"F3.wireOp",EDGE,"E1.sketch_text.stroke-565"),sQuery(id+"F3.wireOp",EDGE,"E1.sketch_text.stroke-566"),sQuery(id+"F3.wireOp",EDGE,"E1.sketch_text.stroke-567"),sQuery(id+"F3.wireOp",EDGE,"E1.sketch_text.stroke-568"),sQuery(id+"F3.wireOp",EDGE,"E1.sketch_text.stroke-569"),sQuery(id+"F3.wireOp",EDGE,"E1.sketch_text.stroke-570"),sQuery(id+"F3.wireOp",EDGE,"E1.sketch_text.stroke-571"),sQuery(id+"F3.wireOp",EDGE,"E1.sketch_text.stroke-572"),sQuery(id+"F3.wireOp",EDGE,"E1.sketch_text.stroke-573"),sQuery(id+"F3.wireOp",EDGE,"E1.sketch_text.stroke-574"),sQuery(id+"F3.wireOp",EDGE,"E1.sketch_text.stroke-575"),sQuery(id+"F3.wireOp",EDGE,"E1.sketch_text.stroke-576"),sQuery(id+"F3.wireOp",EDGE,"E1.sketch_text.stroke-577"),sQuery(id+"F3.wireOp",EDGE,"E1.sketch_text.stroke-578"),sQuery(id+"F3.wireOp",EDGE,"E1.sketch_text.stroke-579"),sQuery(id+"F3.wireOp",EDGE,"E1.sketch_text.stroke-580"),sQuery(id+"F3.wireOp",EDGE,"E1.sketch_text.stroke-581"),sQuery(id+"F3.wireOp",EDGE,"E1.sketch_text.stroke-582"),sQuery(id+"F3.wireOp",EDGE,"E1.sketch_text.stroke-583"),sQuery(id+"F3.wireOp",EDGE,"E1.sketch_text.stroke-584"),sQuery(id+"F3.wireOp",EDGE,"E1.sketch_text.stroke-585"),sQuery(id+"F3.wireOp",EDGE,"E1.sketch_text.stroke-586"),sQuery(id+"F3.wireOp",EDGE,"E1.sketch_text.stroke-587"),sQuery(id+"F3.wireOp",EDGE,"E1.sketch_text.stroke-588"),sQuery(id+"F3.wireOp",EDGE,"E1.sketch_text.stroke-589"),sQuery(id+"F3.wireOp",EDGE,"E1.sketch_text.stroke-590"),sQuery(id+"F3.wireOp",EDGE,"E1.sketch_text.stroke-591"),sQuery(id+"F3.wireOp",EDGE,"E1.sketch_text.stroke-592"),sQuery(id+"F3.wireOp",EDGE,"E1.sketch_text.stroke-593"),sQuery(id+"F3.wireOp",EDGE,"E1.sketch_text.stroke-594"),sQuery(id+"F3.wireOp",EDGE,"E1.sketch_text.stroke-595")])]});
            var Q36;
            Q36=makeQuery(id+"F4.opExtrude","SWEPT_BODY",BODY,{"disambiguationData":[OSD([sQuery(id+"F3.wireOp",EDGE,"E1.sketch_text.stroke-596"),sQuery(id+"F3.wireOp",EDGE,"E1.sketch_text.stroke-597"),sQuery(id+"F3.wireOp",EDGE,"E1.sketch_text.stroke-598"),sQuery(id+"F3.wireOp",EDGE,"E1.sketch_text.stroke-599")])]});
            var Q37;
            Q37=makeQuery(id+"F4.opExtrude","SWEPT_BODY",BODY,{"disambiguationData":[OSD([sQuery(id+"F3.wireOp",EDGE,"E1.sketch_text.stroke-600"),sQuery(id+"F3.wireOp",EDGE,"E1.sketch_text.stroke-601"),sQuery(id+"F3.wireOp",EDGE,"E1.sketch_text.stroke-602"),sQuery(id+"F3.wireOp",EDGE,"E1.sketch_text.stroke-603"),sQuery(id+"F3.wireOp",EDGE,"E1.sketch_text.stroke-604"),sQuery(id+"F3.wireOp",EDGE,"E1.sketch_text.stroke-605"),sQuery(id+"F3.wireOp",EDGE,"E1.sketch_text.stroke-606")])]});
            var Q38;
            Q38=makeQuery(id+"F4.opExtrude","SWEPT_BODY",BODY,{"disambiguationData":[OSD([sQuery(id+"F3.wireOp",EDGE,"E1.sketch_text.stroke-607"),sQuery(id+"F3.wireOp",EDGE,"E1.sketch_text.stroke-608"),sQuery(id+"F3.wireOp",EDGE,"E1.sketch_text.stroke-609"),sQuery(id+"F3.wireOp",EDGE,"E1.sketch_text.stroke-610")])]});
            var Q39;
            Q39=makeQuery(id+"F4.opExtrude","SWEPT_BODY",BODY,{"disambiguationData":[OSD([sQuery(id+"F3.wireOp",EDGE,"E1.sketch_text.stroke-611"),sQuery(id+"F3.wireOp",EDGE,"E1.sketch_text.stroke-612"),sQuery(id+"F3.wireOp",EDGE,"E1.sketch_text.stroke-613"),sQuery(id+"F3.wireOp",EDGE,"E1.sketch_text.stroke-614")])]});
            var Q40;
            Q40=makeQuery(id+"F4.opExtrude","SWEPT_BODY",BODY,{"disambiguationData":[OSD([sQuery(id+"F3.wireOp",EDGE,"E1.sketch_text.stroke-615"),sQuery(id+"F3.wireOp",EDGE,"E1.sketch_text.stroke-616"),sQuery(id+"F3.wireOp",EDGE,"E1.sketch_text.stroke-617"),sQuery(id+"F3.wireOp",EDGE,"E1.sketch_text.stroke-618"),sQuery(id+"F3.wireOp",EDGE,"E1.sketch_text.stroke-619"),sQuery(id+"F3.wireOp",EDGE,"E1.sketch_text.stroke-620"),sQuery(id+"F3.wireOp",EDGE,"E1.sketch_text.stroke-621")])]});
            var Q41;
            Q41=makeQuery(id+"F4.opExtrude","SWEPT_BODY",BODY,{"disambiguationData":[OSD([sQuery(id+"F3.wireOp",EDGE,"E1.sketch_text.stroke-622"),sQuery(id+"F3.wireOp",EDGE,"E1.sketch_text.stroke-623"),sQuery(id+"F3.wireOp",EDGE,"E1.sketch_text.stroke-624"),sQuery(id+"F3.wireOp",EDGE,"E1.sketch_text.stroke-625")])]});
            var Q42;
            Q42=makeQuery(id+"F4.opExtrude","SWEPT_BODY",BODY,{"disambiguationData":[OSD([sQuery(id+"F3.wireOp",EDGE,"E1.sketch_text.stroke-626"),sQuery(id+"F3.wireOp",EDGE,"E1.sketch_text.stroke-627"),sQuery(id+"F3.wireOp",EDGE,"E1.sketch_text.stroke-628"),sQuery(id+"F3.wireOp",EDGE,"E1.sketch_text.stroke-629"),sQuery(id+"F3.wireOp",EDGE,"E1.sketch_text.stroke-630"),sQuery(id+"F3.wireOp",EDGE,"E1.sketch_text.stroke-631"),sQuery(id+"F3.wireOp",EDGE,"E1.sketch_text.stroke-632"),sQuery(id+"F3.wireOp",EDGE,"E1.sketch_text.stroke-633"),sQuery(id+"F3.wireOp",EDGE,"E1.sketch_text.stroke-634"),sQuery(id+"F3.wireOp",EDGE,"E1.sketch_text.stroke-635"),sQuery(id+"F3.wireOp",EDGE,"E1.sketch_text.stroke-636"),sQuery(id+"F3.wireOp",EDGE,"E1.sketch_text.stroke-637"),sQuery(id+"F3.wireOp",EDGE,"E1.sketch_text.stroke-638"),sQuery(id+"F3.wireOp",EDGE,"E1.sketch_text.stroke-639"),sQuery(id+"F3.wireOp",EDGE,"E1.sketch_text.stroke-640"),sQuery(id+"F3.wireOp",EDGE,"E1.sketch_text.stroke-641"),sQuery(id+"F3.wireOp",EDGE,"E1.sketch_text.stroke-642"),sQuery(id+"F3.wireOp",EDGE,"E1.sketch_text.stroke-643")])]});
            var Q43;
            Q43=makeQuery(id+"F4.opExtrude","SWEPT_BODY",BODY,{"disambiguationData":[OSD([sQuery(id+"F3.wireOp",EDGE,"E1.sketch_text.stroke-644"),sQuery(id+"F3.wireOp",EDGE,"E1.sketch_text.stroke-645"),sQuery(id+"F3.wireOp",EDGE,"E1.sketch_text.stroke-646"),sQuery(id+"F3.wireOp",EDGE,"E1.sketch_text.stroke-647"),sQuery(id+"F3.wireOp",EDGE,"E1.sketch_text.stroke-648"),sQuery(id+"F3.wireOp",EDGE,"E1.sketch_text.stroke-649"),sQuery(id+"F3.wireOp",EDGE,"E1.sketch_text.stroke-650"),sQuery(id+"F3.wireOp",EDGE,"E1.sketch_text.stroke-651"),sQuery(id+"F3.wireOp",EDGE,"E1.sketch_text.stroke-652"),sQuery(id+"F3.wireOp",EDGE,"E1.sketch_text.stroke-653"),sQuery(id+"F3.wireOp",EDGE,"E1.sketch_text.stroke-654"),sQuery(id+"F3.wireOp",EDGE,"E1.sketch_text.stroke-655"),sQuery(id+"F3.wireOp",EDGE,"E1.sketch_text.stroke-656"),sQuery(id+"F3.wireOp",EDGE,"E1.sketch_text.stroke-657"),sQuery(id+"F3.wireOp",EDGE,"E1.sketch_text.stroke-658"),sQuery(id+"F3.wireOp",EDGE,"E1.sketch_text.stroke-659"),sQuery(id+"F3.wireOp",EDGE,"E1.sketch_text.stroke-660"),sQuery(id+"F3.wireOp",EDGE,"E1.sketch_text.stroke-661")])]});
            var Q44;
            Q44=makeQuery(id+"F4.opExtrude","SWEPT_BODY",BODY,{"disambiguationData":[OSD([sQuery(id+"F3.wireOp",EDGE,"E1.sketch_text.stroke-662"),sQuery(id+"F3.wireOp",EDGE,"E1.sketch_text.stroke-663"),sQuery(id+"F3.wireOp",EDGE,"E1.sketch_text.stroke-664"),sQuery(id+"F3.wireOp",EDGE,"E1.sketch_text.stroke-665"),sQuery(id+"F3.wireOp",EDGE,"E1.sketch_text.stroke-666"),sQuery(id+"F3.wireOp",EDGE,"E1.sketch_text.stroke-667"),sQuery(id+"F3.wireOp",EDGE,"E1.sketch_text.stroke-668"),sQuery(id+"F3.wireOp",EDGE,"E1.sketch_text.stroke-669"),sQuery(id+"F3.wireOp",EDGE,"E1.sketch_text.stroke-670"),sQuery(id+"F3.wireOp",EDGE,"E1.sketch_text.stroke-671"),sQuery(id+"F3.wireOp",EDGE,"E1.sketch_text.stroke-672")])]});
            var Q45;
            Q45=makeQuery(id+"F4.opExtrude","SWEPT_BODY",BODY,{"disambiguationData":[OSD([sQuery(id+"F3.wireOp",EDGE,"E1.sketch_text.stroke-673"),sQuery(id+"F3.wireOp",EDGE,"E1.sketch_text.stroke-674"),sQuery(id+"F3.wireOp",EDGE,"E1.sketch_text.stroke-675"),sQuery(id+"F3.wireOp",EDGE,"E1.sketch_text.stroke-676"),sQuery(id+"F3.wireOp",EDGE,"E1.sketch_text.stroke-677"),sQuery(id+"F3.wireOp",EDGE,"E1.sketch_text.stroke-678"),sQuery(id+"F3.wireOp",EDGE,"E1.sketch_text.stroke-679"),sQuery(id+"F3.wireOp",EDGE,"E1.sketch_text.stroke-680"),sQuery(id+"F3.wireOp",EDGE,"E1.sketch_text.stroke-681"),sQuery(id+"F3.wireOp",EDGE,"E1.sketch_text.stroke-682"),sQuery(id+"F3.wireOp",EDGE,"E1.sketch_text.stroke-683"),sQuery(id+"F3.wireOp",EDGE,"E1.sketch_text.stroke-684"),sQuery(id+"F3.wireOp",EDGE,"E1.sketch_text.stroke-685"),sQuery(id+"F3.wireOp",EDGE,"E1.sketch_text.stroke-686")])]});
            var Q46;
            Q46=makeQuery(id+"F4.opExtrude","SWEPT_BODY",BODY,{"disambiguationData":[OSD([sQuery(id+"F3.wireOp",EDGE,"E1.sketch_text.stroke-687"),sQuery(id+"F3.wireOp",EDGE,"E1.sketch_text.stroke-688"),sQuery(id+"F3.wireOp",EDGE,"E1.sketch_text.stroke-689"),sQuery(id+"F3.wireOp",EDGE,"E1.sketch_text.stroke-690"),sQuery(id+"F3.wireOp",EDGE,"E1.sketch_text.stroke-691"),sQuery(id+"F3.wireOp",EDGE,"E1.sketch_text.stroke-692"),sQuery(id+"F3.wireOp",EDGE,"E1.sketch_text.stroke-693"),sQuery(id+"F3.wireOp",EDGE,"E1.sketch_text.stroke-694"),sQuery(id+"F3.wireOp",EDGE,"E1.sketch_text.stroke-695"),sQuery(id+"F3.wireOp",EDGE,"E1.sketch_text.stroke-696"),sQuery(id+"F3.wireOp",EDGE,"E1.sketch_text.stroke-697"),sQuery(id+"F3.wireOp",EDGE,"E1.sketch_text.stroke-698")])]});
            var Q47;
            Q47=makeQuery(id+"F4.opExtrude","SWEPT_BODY",BODY,{"disambiguationData":[OSD([sQuery(id+"F3.wireOp",EDGE,"E1.sketch_text.stroke-699"),sQuery(id+"F3.wireOp",EDGE,"E1.sketch_text.stroke-700"),sQuery(id+"F3.wireOp",EDGE,"E1.sketch_text.stroke-701"),sQuery(id+"F3.wireOp",EDGE,"E1.sketch_text.stroke-702"),sQuery(id+"F3.wireOp",EDGE,"E1.sketch_text.stroke-703"),sQuery(id+"F3.wireOp",EDGE,"E1.sketch_text.stroke-704"),sQuery(id+"F3.wireOp",EDGE,"E1.sketch_text.stroke-705"),sQuery(id+"F3.wireOp",EDGE,"E1.sketch_text.stroke-706"),sQuery(id+"F3.wireOp",EDGE,"E1.sketch_text.stroke-707"),sQuery(id+"F3.wireOp",EDGE,"E1.sketch_text.stroke-708"),sQuery(id+"F3.wireOp",EDGE,"E1.sketch_text.stroke-709"),sQuery(id+"F3.wireOp",EDGE,"E1.sketch_text.stroke-710"),sQuery(id+"F3.wireOp",EDGE,"E1.sketch_text.stroke-711")])]});
            var Q48;
            Q48=makeQuery(id+"F4.opExtrude","SWEPT_BODY",BODY,{"disambiguationData":[OSD([sQuery(id+"F3.wireOp",EDGE,"E1.sketch_text.stroke-712"),sQuery(id+"F3.wireOp",EDGE,"E1.sketch_text.stroke-713"),sQuery(id+"F3.wireOp",EDGE,"E1.sketch_text.stroke-714"),sQuery(id+"F3.wireOp",EDGE,"E1.sketch_text.stroke-715"),sQuery(id+"F3.wireOp",EDGE,"E1.sketch_text.stroke-716"),sQuery(id+"F3.wireOp",EDGE,"E1.sketch_text.stroke-717"),sQuery(id+"F3.wireOp",EDGE,"E1.sketch_text.stroke-718"),sQuery(id+"F3.wireOp",EDGE,"E1.sketch_text.stroke-719"),sQuery(id+"F3.wireOp",EDGE,"E1.sketch_text.stroke-720"),sQuery(id+"F3.wireOp",EDGE,"E1.sketch_text.stroke-721"),sQuery(id+"F3.wireOp",EDGE,"E1.sketch_text.stroke-722"),sQuery(id+"F3.wireOp",EDGE,"E1.sketch_text.stroke-723"),sQuery(id+"F3.wireOp",EDGE,"E1.sketch_text.stroke-724"),sQuery(id+"F3.wireOp",EDGE,"E1.sketch_text.stroke-725"),sQuery(id+"F3.wireOp",EDGE,"E1.sketch_text.stroke-726"),sQuery(id+"F3.wireOp",EDGE,"E1.sketch_text.stroke-727"),sQuery(id+"F3.wireOp",EDGE,"E1.sketch_text.stroke-728"),sQuery(id+"F3.wireOp",EDGE,"E1.sketch_text.stroke-729"),sQuery(id+"F3.wireOp",EDGE,"E1.sketch_text.stroke-730"),sQuery(id+"F3.wireOp",EDGE,"E1.sketch_text.stroke-731"),sQuery(id+"F3.wireOp",EDGE,"E1.sketch_text.stroke-732"),sQuery(id+"F3.wireOp",EDGE,"E1.sketch_text.stroke-733"),sQuery(id+"F3.wireOp",EDGE,"E1.sketch_text.stroke-734"),sQuery(id+"F3.wireOp",EDGE,"E1.sketch_text.stroke-735"),sQuery(id+"F3.wireOp",EDGE,"E1.sketch_text.stroke-736")])]});
            var Q49;
            Q49=makeQuery(id+"F4.opExtrude","SWEPT_BODY",BODY,{"disambiguationData":[OSD([sQuery(id+"F3.wireOp",EDGE,"E1.sketch_text.stroke-737"),sQuery(id+"F3.wireOp",EDGE,"E1.sketch_text.stroke-738"),sQuery(id+"F3.wireOp",EDGE,"E1.sketch_text.stroke-739"),sQuery(id+"F3.wireOp",EDGE,"E1.sketch_text.stroke-740"),sQuery(id+"F3.wireOp",EDGE,"E1.sketch_text.stroke-741"),sQuery(id+"F3.wireOp",EDGE,"E1.sketch_text.stroke-742"),sQuery(id+"F3.wireOp",EDGE,"E1.sketch_text.stroke-743"),sQuery(id+"F3.wireOp",EDGE,"E1.sketch_text.stroke-744"),sQuery(id+"F3.wireOp",EDGE,"E1.sketch_text.stroke-745"),sQuery(id+"F3.wireOp",EDGE,"E1.sketch_text.stroke-746"),sQuery(id+"F3.wireOp",EDGE,"E1.sketch_text.stroke-747"),sQuery(id+"F3.wireOp",EDGE,"E1.sketch_text.stroke-748"),sQuery(id+"F3.wireOp",EDGE,"E1.sketch_text.stroke-749"),sQuery(id+"F3.wireOp",EDGE,"E1.sketch_text.stroke-750"),sQuery(id+"F3.wireOp",EDGE,"E1.sketch_text.stroke-751"),sQuery(id+"F3.wireOp",EDGE,"E1.sketch_text.stroke-752"),sQuery(id+"F3.wireOp",EDGE,"E1.sketch_text.stroke-753"),sQuery(id+"F3.wireOp",EDGE,"E1.sketch_text.stroke-754"),sQuery(id+"F3.wireOp",EDGE,"E1.sketch_text.stroke-755")])]});
            var Q50;
            Q50=makeQuery(id+"F4.opExtrude","SWEPT_BODY",BODY,{"disambiguationData":[OSD([sQuery(id+"F3.wireOp",EDGE,"E1.sketch_text.stroke-756"),sQuery(id+"F3.wireOp",EDGE,"E1.sketch_text.stroke-757"),sQuery(id+"F3.wireOp",EDGE,"E1.sketch_text.stroke-758"),sQuery(id+"F3.wireOp",EDGE,"E1.sketch_text.stroke-759"),sQuery(id+"F3.wireOp",EDGE,"E1.sketch_text.stroke-760"),sQuery(id+"F3.wireOp",EDGE,"E1.sketch_text.stroke-761"),sQuery(id+"F3.wireOp",EDGE,"E1.sketch_text.stroke-762"),sQuery(id+"F3.wireOp",EDGE,"E1.sketch_text.stroke-763"),sQuery(id+"F3.wireOp",EDGE,"E1.sketch_text.stroke-764"),sQuery(id+"F3.wireOp",EDGE,"E1.sketch_text.stroke-765"),sQuery(id+"F3.wireOp",EDGE,"E1.sketch_text.stroke-766"),sQuery(id+"F3.wireOp",EDGE,"E1.sketch_text.stroke-767"),sQuery(id+"F3.wireOp",EDGE,"E1.sketch_text.stroke-768"),sQuery(id+"F3.wireOp",EDGE,"E1.sketch_text.stroke-769"),sQuery(id+"F3.wireOp",EDGE,"E1.sketch_text.stroke-770"),sQuery(id+"F3.wireOp",EDGE,"E1.sketch_text.stroke-771"),sQuery(id+"F3.wireOp",EDGE,"E1.sketch_text.stroke-772"),sQuery(id+"F3.wireOp",EDGE,"E1.sketch_text.stroke-773"),sQuery(id+"F3.wireOp",EDGE,"E1.sketch_text.stroke-774"),sQuery(id+"F3.wireOp",EDGE,"E1.sketch_text.stroke-775"),sQuery(id+"F3.wireOp",EDGE,"E1.sketch_text.stroke-776"),sQuery(id+"F3.wireOp",EDGE,"E1.sketch_text.stroke-777"),sQuery(id+"F3.wireOp",EDGE,"E1.sketch_text.stroke-778"),sQuery(id+"F3.wireOp",EDGE,"E1.sketch_text.stroke-779"),sQuery(id+"F3.wireOp",EDGE,"E1.sketch_text.stroke-780"),sQuery(id+"F3.wireOp",EDGE,"E1.sketch_text.stroke-781"),sQuery(id+"F3.wireOp",EDGE,"E1.sketch_text.stroke-782"),sQuery(id+"F3.wireOp",EDGE,"E1.sketch_text.stroke-783"),sQuery(id+"F3.wireOp",EDGE,"E1.sketch_text.stroke-784"),sQuery(id+"F3.wireOp",EDGE,"E1.sketch_text.stroke-785"),sQuery(id+"F3.wireOp",EDGE,"E1.sketch_text.stroke-786"),sQuery(id+"F3.wireOp",EDGE,"E1.sketch_text.stroke-787"),sQuery(id+"F3.wireOp",EDGE,"E1.sketch_text.stroke-788"),sQuery(id+"F3.wireOp",EDGE,"E1.sketch_text.stroke-789"),sQuery(id+"F3.wireOp",EDGE,"E1.sketch_text.stroke-790"),sQuery(id+"F3.wireOp",EDGE,"E1.sketch_text.stroke-791")])]});
            var Q51;
            Q51=makeQuery(id+"F4.opExtrude","SWEPT_BODY",BODY,{"disambiguationData":[OSD([sQuery(id+"F3.wireOp",EDGE,"E1.sketch_text.stroke-792"),sQuery(id+"F3.wireOp",EDGE,"E1.sketch_text.stroke-793"),sQuery(id+"F3.wireOp",EDGE,"E1.sketch_text.stroke-794"),sQuery(id+"F3.wireOp",EDGE,"E1.sketch_text.stroke-795"),sQuery(id+"F3.wireOp",EDGE,"E1.sketch_text.stroke-796"),sQuery(id+"F3.wireOp",EDGE,"E1.sketch_text.stroke-797"),sQuery(id+"F3.wireOp",EDGE,"E1.sketch_text.stroke-798")])]});
            var Q52;
            Q52=makeQuery(id+"F4.opExtrude","SWEPT_BODY",BODY,{"disambiguationData":[OSD([sQuery(id+"F3.wireOp",EDGE,"E1.sketch_text.stroke-799"),sQuery(id+"F3.wireOp",EDGE,"E1.sketch_text.stroke-800"),sQuery(id+"F3.wireOp",EDGE,"E1.sketch_text.stroke-801"),sQuery(id+"F3.wireOp",EDGE,"E1.sketch_text.stroke-802"),sQuery(id+"F3.wireOp",EDGE,"E1.sketch_text.stroke-803"),sQuery(id+"F3.wireOp",EDGE,"E1.sketch_text.stroke-804"),sQuery(id+"F3.wireOp",EDGE,"E1.sketch_text.stroke-805")])]});
            var Q53;
            Q53=makeQuery(id+"F4.opExtrude","SWEPT_BODY",BODY,{"disambiguationData":[OSD([sQuery(id+"F3.wireOp",EDGE,"E1.sketch_text.stroke-806"),sQuery(id+"F3.wireOp",EDGE,"E1.sketch_text.stroke-807"),sQuery(id+"F3.wireOp",EDGE,"E1.sketch_text.stroke-808"),sQuery(id+"F3.wireOp",EDGE,"E1.sketch_text.stroke-809"),sQuery(id+"F3.wireOp",EDGE,"E1.sketch_text.stroke-810"),sQuery(id+"F3.wireOp",EDGE,"E1.sketch_text.stroke-811"),sQuery(id+"F3.wireOp",EDGE,"E1.sketch_text.stroke-812"),sQuery(id+"F3.wireOp",EDGE,"E1.sketch_text.stroke-813")])]});
            var Q54;
            Q54=makeQuery(id+"F4.opExtrude","SWEPT_BODY",BODY,{"disambiguationData":[OSD([sQuery(id+"F3.wireOp",EDGE,"E1.sketch_text.stroke-814"),sQuery(id+"F3.wireOp",EDGE,"E1.sketch_text.stroke-815"),sQuery(id+"F3.wireOp",EDGE,"E1.sketch_text.stroke-816"),sQuery(id+"F3.wireOp",EDGE,"E1.sketch_text.stroke-817"),sQuery(id+"F3.wireOp",EDGE,"E1.sketch_text.stroke-818"),sQuery(id+"F3.wireOp",EDGE,"E1.sketch_text.stroke-819"),sQuery(id+"F3.wireOp",EDGE,"E1.sketch_text.stroke-820"),sQuery(id+"F3.wireOp",EDGE,"E1.sketch_text.stroke-821"),sQuery(id+"F3.wireOp",EDGE,"E1.sketch_text.stroke-822"),sQuery(id+"F3.wireOp",EDGE,"E1.sketch_text.stroke-823"),sQuery(id+"F3.wireOp",EDGE,"E1.sketch_text.stroke-824"),sQuery(id+"F3.wireOp",EDGE,"E1.sketch_text.stroke-825"),sQuery(id+"F3.wireOp",EDGE,"E1.sketch_text.stroke-826"),sQuery(id+"F3.wireOp",EDGE,"E1.sketch_text.stroke-827"),sQuery(id+"F3.wireOp",EDGE,"E1.sketch_text.stroke-828"),sQuery(id+"F3.wireOp",EDGE,"E1.sketch_text.stroke-829"),sQuery(id+"F3.wireOp",EDGE,"E1.sketch_text.stroke-830"),sQuery(id+"F3.wireOp",EDGE,"E1.sketch_text.stroke-831")])]});
            var Q55;
            Q55=makeQuery(id+"F4.opExtrude","SWEPT_BODY",BODY,{"disambiguationData":[OSD([sQuery(id+"F3.wireOp",EDGE,"E1.sketch_text.stroke-832"),sQuery(id+"F3.wireOp",EDGE,"E1.sketch_text.stroke-833"),sQuery(id+"F3.wireOp",EDGE,"E1.sketch_text.stroke-834"),sQuery(id+"F3.wireOp",EDGE,"E1.sketch_text.stroke-835"),sQuery(id+"F3.wireOp",EDGE,"E1.sketch_text.stroke-836"),sQuery(id+"F3.wireOp",EDGE,"E1.sketch_text.stroke-837"),sQuery(id+"F3.wireOp",EDGE,"E1.sketch_text.stroke-838"),sQuery(id+"F3.wireOp",EDGE,"E1.sketch_text.stroke-839"),sQuery(id+"F3.wireOp",EDGE,"E1.sketch_text.stroke-840"),sQuery(id+"F3.wireOp",EDGE,"E1.sketch_text.stroke-841"),sQuery(id+"F3.wireOp",EDGE,"E1.sketch_text.stroke-842"),sQuery(id+"F3.wireOp",EDGE,"E1.sketch_text.stroke-843"),sQuery(id+"F3.wireOp",EDGE,"E1.sketch_text.stroke-844"),sQuery(id+"F3.wireOp",EDGE,"E1.sketch_text.stroke-845"),sQuery(id+"F3.wireOp",EDGE,"E1.sketch_text.stroke-846")])]});
            var Q56;
            Q56=makeQuery(id+"F4.opExtrude","SWEPT_BODY",BODY,{"disambiguationData":[OSD([sQuery(id+"F3.wireOp",EDGE,"E1.sketch_text.stroke-847"),sQuery(id+"F3.wireOp",EDGE,"E1.sketch_text.stroke-848"),sQuery(id+"F3.wireOp",EDGE,"E1.sketch_text.stroke-849"),sQuery(id+"F3.wireOp",EDGE,"E1.sketch_text.stroke-850"),sQuery(id+"F3.wireOp",EDGE,"E1.sketch_text.stroke-851"),sQuery(id+"F3.wireOp",EDGE,"E1.sketch_text.stroke-852"),sQuery(id+"F3.wireOp",EDGE,"E1.sketch_text.stroke-853"),sQuery(id+"F3.wireOp",EDGE,"E1.sketch_text.stroke-854"),sQuery(id+"F3.wireOp",EDGE,"E1.sketch_text.stroke-855"),sQuery(id+"F3.wireOp",EDGE,"E1.sketch_text.stroke-856"),sQuery(id+"F3.wireOp",EDGE,"E1.sketch_text.stroke-857"),sQuery(id+"F3.wireOp",EDGE,"E1.sketch_text.stroke-858"),sQuery(id+"F3.wireOp",EDGE,"E1.sketch_text.stroke-859"),sQuery(id+"F3.wireOp",EDGE,"E1.sketch_text.stroke-860"),sQuery(id+"F3.wireOp",EDGE,"E1.sketch_text.stroke-861"),sQuery(id+"F3.wireOp",EDGE,"E1.sketch_text.stroke-862"),sQuery(id+"F3.wireOp",EDGE,"E1.sketch_text.stroke-863"),sQuery(id+"F3.wireOp",EDGE,"E1.sketch_text.stroke-864"),sQuery(id+"F3.wireOp",EDGE,"E1.sketch_text.stroke-865")])]});
            var Q57;
            Q57=makeQuery(id+"F4.opExtrude","SWEPT_BODY",BODY,{"disambiguationData":[OSD([sQuery(id+"F3.wireOp",EDGE,"E1.sketch_text.stroke-866"),sQuery(id+"F3.wireOp",EDGE,"E1.sketch_text.stroke-867"),sQuery(id+"F3.wireOp",EDGE,"E1.sketch_text.stroke-868"),sQuery(id+"F3.wireOp",EDGE,"E1.sketch_text.stroke-869"),sQuery(id+"F3.wireOp",EDGE,"E1.sketch_text.stroke-870"),sQuery(id+"F3.wireOp",EDGE,"E1.sketch_text.stroke-871"),sQuery(id+"F3.wireOp",EDGE,"E1.sketch_text.stroke-872"),sQuery(id+"F3.wireOp",EDGE,"E1.sketch_text.stroke-873"),sQuery(id+"F3.wireOp",EDGE,"E1.sketch_text.stroke-874"),sQuery(id+"F3.wireOp",EDGE,"E1.sketch_text.stroke-875"),sQuery(id+"F3.wireOp",EDGE,"E1.sketch_text.stroke-876"),sQuery(id+"F3.wireOp",EDGE,"E1.sketch_text.stroke-877"),sQuery(id+"F3.wireOp",EDGE,"E1.sketch_text.stroke-878"),sQuery(id+"F3.wireOp",EDGE,"E1.sketch_text.stroke-879"),sQuery(id+"F3.wireOp",EDGE,"E1.sketch_text.stroke-880"),sQuery(id+"F3.wireOp",EDGE,"E1.sketch_text.stroke-881"),sQuery(id+"F3.wireOp",EDGE,"E1.sketch_text.stroke-882"),sQuery(id+"F3.wireOp",EDGE,"E1.sketch_text.stroke-883"),sQuery(id+"F3.wireOp",EDGE,"E1.sketch_text.stroke-884"),sQuery(id+"F3.wireOp",EDGE,"E1.sketch_text.stroke-885"),sQuery(id+"F3.wireOp",EDGE,"E1.sketch_text.stroke-886"),sQuery(id+"F3.wireOp",EDGE,"E1.sketch_text.stroke-887"),sQuery(id+"F3.wireOp",EDGE,"E1.sketch_text.stroke-888"),sQuery(id+"F3.wireOp",EDGE,"E1.sketch_text.stroke-889"),sQuery(id+"F3.wireOp",EDGE,"E1.sketch_text.stroke-890"),sQuery(id+"F3.wireOp",EDGE,"E1.sketch_text.stroke-891"),sQuery(id+"F3.wireOp",EDGE,"E1.sketch_text.stroke-892"),sQuery(id+"F3.wireOp",EDGE,"E1.sketch_text.stroke-893"),sQuery(id+"F3.wireOp",EDGE,"E1.sketch_text.stroke-894"),sQuery(id+"F3.wireOp",EDGE,"E1.sketch_text.stroke-895"),sQuery(id+"F3.wireOp",EDGE,"E1.sketch_text.stroke-896"),sQuery(id+"F3.wireOp",EDGE,"E1.sketch_text.stroke-897"),sQuery(id+"F3.wireOp",EDGE,"E1.sketch_text.stroke-898"),sQuery(id+"F3.wireOp",EDGE,"E1.sketch_text.stroke-899"),sQuery(id+"F3.wireOp",EDGE,"E1.sketch_text.stroke-900"),sQuery(id+"F3.wireOp",EDGE,"E1.sketch_text.stroke-901")])]});
            var Q58;
            Q58=makeQuery(id+"F4.opExtrude","SWEPT_BODY",BODY,{"disambiguationData":[OSD([sQuery(id+"F3.wireOp",EDGE,"E1.sketch_text.stroke-902"),sQuery(id+"F3.wireOp",EDGE,"E1.sketch_text.stroke-903"),sQuery(id+"F3.wireOp",EDGE,"E1.sketch_text.stroke-904"),sQuery(id+"F3.wireOp",EDGE,"E1.sketch_text.stroke-905"),sQuery(id+"F3.wireOp",EDGE,"E1.sketch_text.stroke-906")])]});
            var Q59;
            Q59=makeQuery(id+"F4.opExtrude","SWEPT_BODY",BODY,{"disambiguationData":[OSD([sQuery(id+"F3.wireOp",EDGE,"E1.sketch_text.stroke-907"),sQuery(id+"F3.wireOp",EDGE,"E1.sketch_text.stroke-908"),sQuery(id+"F3.wireOp",EDGE,"E1.sketch_text.stroke-909"),sQuery(id+"F3.wireOp",EDGE,"E1.sketch_text.stroke-910"),sQuery(id+"F3.wireOp",EDGE,"E1.sketch_text.stroke-911"),sQuery(id+"F3.wireOp",EDGE,"E1.sketch_text.stroke-912"),sQuery(id+"F3.wireOp",EDGE,"E1.sketch_text.stroke-913"),sQuery(id+"F3.wireOp",EDGE,"E1.sketch_text.stroke-914"),sQuery(id+"F3.wireOp",EDGE,"E1.sketch_text.stroke-915"),sQuery(id+"F3.wireOp",EDGE,"E1.sketch_text.stroke-916"),sQuery(id+"F3.wireOp",EDGE,"E1.sketch_text.stroke-917"),sQuery(id+"F3.wireOp",EDGE,"E1.sketch_text.stroke-918"),sQuery(id+"F3.wireOp",EDGE,"E1.sketch_text.stroke-919"),sQuery(id+"F3.wireOp",EDGE,"E1.sketch_text.stroke-920"),sQuery(id+"F3.wireOp",EDGE,"E1.sketch_text.stroke-921"),sQuery(id+"F3.wireOp",EDGE,"E1.sketch_text.stroke-922")])]});
            var Q60;
            Q60=makeQuery(id+"F4.opExtrude","SWEPT_BODY",BODY,{"disambiguationData":[OSD([sQuery(id+"F3.wireOp",EDGE,"E1.sketch_text.stroke-923"),sQuery(id+"F3.wireOp",EDGE,"E1.sketch_text.stroke-924"),sQuery(id+"F3.wireOp",EDGE,"E1.sketch_text.stroke-925"),sQuery(id+"F3.wireOp",EDGE,"E1.sketch_text.stroke-926"),sQuery(id+"F3.wireOp",EDGE,"E1.sketch_text.stroke-927"),sQuery(id+"F3.wireOp",EDGE,"E1.sketch_text.stroke-928"),sQuery(id+"F3.wireOp",EDGE,"E1.sketch_text.stroke-929"),sQuery(id+"F3.wireOp",EDGE,"E1.sketch_text.stroke-930"),sQuery(id+"F3.wireOp",EDGE,"E1.sketch_text.stroke-931"),sQuery(id+"F3.wireOp",EDGE,"E1.sketch_text.stroke-932"),sQuery(id+"F3.wireOp",EDGE,"E1.sketch_text.stroke-933"),sQuery(id+"F3.wireOp",EDGE,"E1.sketch_text.stroke-934"),sQuery(id+"F3.wireOp",EDGE,"E1.sketch_text.stroke-935"),sQuery(id+"F3.wireOp",EDGE,"E1.sketch_text.stroke-936"),sQuery(id+"F3.wireOp",EDGE,"E1.sketch_text.stroke-937"),sQuery(id+"F3.wireOp",EDGE,"E1.sketch_text.stroke-938"),sQuery(id+"F3.wireOp",EDGE,"E1.sketch_text.stroke-939"),sQuery(id+"F3.wireOp",EDGE,"E1.sketch_text.stroke-940")])]});
            var Q61;
            Q61=makeQuery(id+"F4.opExtrude","SWEPT_BODY",BODY,{"disambiguationData":[OSD([sQuery(id+"F3.wireOp",EDGE,"E1.sketch_text.stroke-941"),sQuery(id+"F3.wireOp",EDGE,"E1.sketch_text.stroke-942"),sQuery(id+"F3.wireOp",EDGE,"E1.sketch_text.stroke-943"),sQuery(id+"F3.wireOp",EDGE,"E1.sketch_text.stroke-944"),sQuery(id+"F3.wireOp",EDGE,"E1.sketch_text.stroke-945"),sQuery(id+"F3.wireOp",EDGE,"E1.sketch_text.stroke-946"),sQuery(id+"F3.wireOp",EDGE,"E1.sketch_text.stroke-947"),sQuery(id+"F3.wireOp",EDGE,"E1.sketch_text.stroke-948"),sQuery(id+"F3.wireOp",EDGE,"E1.sketch_text.stroke-949"),sQuery(id+"F3.wireOp",EDGE,"E1.sketch_text.stroke-950"),sQuery(id+"F3.wireOp",EDGE,"E1.sketch_text.stroke-951"),sQuery(id+"F3.wireOp",EDGE,"E1.sketch_text.stroke-952"),sQuery(id+"F3.wireOp",EDGE,"E1.sketch_text.stroke-953")])]});
            var Q62;
            Q62=makeQuery(id+"F4.opExtrude","SWEPT_BODY",BODY,{"disambiguationData":[OSD([sQuery(id+"F3.wireOp",EDGE,"E1.sketch_text.stroke-954"),sQuery(id+"F3.wireOp",EDGE,"E1.sketch_text.stroke-955"),sQuery(id+"F3.wireOp",EDGE,"E1.sketch_text.stroke-956"),sQuery(id+"F3.wireOp",EDGE,"E1.sketch_text.stroke-957"),sQuery(id+"F3.wireOp",EDGE,"E1.sketch_text.stroke-958"),sQuery(id+"F3.wireOp",EDGE,"E1.sketch_text.stroke-959"),sQuery(id+"F3.wireOp",EDGE,"E1.sketch_text.stroke-960"),sQuery(id+"F3.wireOp",EDGE,"E1.sketch_text.stroke-961"),sQuery(id+"F3.wireOp",EDGE,"E1.sketch_text.stroke-962"),sQuery(id+"F3.wireOp",EDGE,"E1.sketch_text.stroke-963"),sQuery(id+"F3.wireOp",EDGE,"E1.sketch_text.stroke-964"),sQuery(id+"F3.wireOp",EDGE,"E1.sketch_text.stroke-965"),sQuery(id+"F3.wireOp",EDGE,"E1.sketch_text.stroke-966"),sQuery(id+"F3.wireOp",EDGE,"E1.sketch_text.stroke-967"),sQuery(id+"F3.wireOp",EDGE,"E1.sketch_text.stroke-968"),sQuery(id+"F3.wireOp",EDGE,"E1.sketch_text.stroke-969"),sQuery(id+"F3.wireOp",EDGE,"E1.sketch_text.stroke-970"),sQuery(id+"F3.wireOp",EDGE,"E1.sketch_text.stroke-971"),sQuery(id+"F3.wireOp",EDGE,"E1.sketch_text.stroke-972"),sQuery(id+"F3.wireOp",EDGE,"E1.sketch_text.stroke-973"),sQuery(id+"F3.wireOp",EDGE,"E1.sketch_text.stroke-974"),sQuery(id+"F3.wireOp",EDGE,"E1.sketch_text.stroke-975"),sQuery(id+"F3.wireOp",EDGE,"E1.sketch_text.stroke-976"),sQuery(id+"F3.wireOp",EDGE,"E1.sketch_text.stroke-977")])]});
            var Q63;
            Q63=makeQuery(id+"F4.opExtrude","SWEPT_BODY",BODY,{"disambiguationData":[OSD([sQuery(id+"F3.wireOp",EDGE,"E1.sketch_text.stroke-978"),sQuery(id+"F3.wireOp",EDGE,"E1.sketch_text.stroke-979"),sQuery(id+"F3.wireOp",EDGE,"E1.sketch_text.stroke-980"),sQuery(id+"F3.wireOp",EDGE,"E1.sketch_text.stroke-981")])]});
            var Q64;
            Q64=makeQuery(id+"F4.opExtrude","SWEPT_BODY",BODY,{"disambiguationData":[OSD([sQuery(id+"F3.wireOp",EDGE,"E1.sketch_text.stroke-982"),sQuery(id+"F3.wireOp",EDGE,"E1.sketch_text.stroke-983"),sQuery(id+"F3.wireOp",EDGE,"E1.sketch_text.stroke-984"),sQuery(id+"F3.wireOp",EDGE,"E1.sketch_text.stroke-985")])]});
            var Q65;
            Q65=makeQuery(id+"F4.opExtrude","SWEPT_BODY",BODY,{"disambiguationData":[OSD([sQuery(id+"F3.wireOp",EDGE,"E1.sketch_text.stroke-986"),sQuery(id+"F3.wireOp",EDGE,"E1.sketch_text.stroke-987"),sQuery(id+"F3.wireOp",EDGE,"E1.sketch_text.stroke-988"),sQuery(id+"F3.wireOp",EDGE,"E1.sketch_text.stroke-989")])]});
            var Q66;
            Q66=makeQuery(id+"F4.opExtrude","SWEPT_BODY",BODY,{"disambiguationData":[OSD([sQuery(id+"F3.wireOp",EDGE,"E1.sketch_text.stroke-990"),sQuery(id+"F3.wireOp",EDGE,"E1.sketch_text.stroke-991"),sQuery(id+"F3.wireOp",EDGE,"E1.sketch_text.stroke-992"),sQuery(id+"F3.wireOp",EDGE,"E1.sketch_text.stroke-993"),sQuery(id+"F3.wireOp",EDGE,"E1.sketch_text.stroke-994"),sQuery(id+"F3.wireOp",EDGE,"E1.sketch_text.stroke-995"),sQuery(id+"F3.wireOp",EDGE,"E1.sketch_text.stroke-996"),sQuery(id+"F3.wireOp",EDGE,"E1.sketch_text.stroke-997"),sQuery(id+"F3.wireOp",EDGE,"E1.sketch_text.stroke-998"),sQuery(id+"F3.wireOp",EDGE,"E1.sketch_text.stroke-999"),sQuery(id+"F3.wireOp",EDGE,"E1.sketch_text.stroke-1000"),sQuery(id+"F3.wireOp",EDGE,"E1.sketch_text.stroke-1001"),sQuery(id+"F3.wireOp",EDGE,"E1.sketch_text.stroke-1002")])]});
            var Q67;
            Q67=makeQuery(id+"F4.opExtrude","SWEPT_BODY",BODY,{"disambiguationData":[OSD([sQuery(id+"F3.wireOp",EDGE,"E1.sketch_text.stroke-1003"),sQuery(id+"F3.wireOp",EDGE,"E1.sketch_text.stroke-1004"),sQuery(id+"F3.wireOp",EDGE,"E1.sketch_text.stroke-1005"),sQuery(id+"F3.wireOp",EDGE,"E1.sketch_text.stroke-1006"),sQuery(id+"F3.wireOp",EDGE,"E1.sketch_text.stroke-1007"),sQuery(id+"F3.wireOp",EDGE,"E1.sketch_text.stroke-1008"),sQuery(id+"F3.wireOp",EDGE,"E1.sketch_text.stroke-1009"),sQuery(id+"F3.wireOp",EDGE,"E1.sketch_text.stroke-1010"),sQuery(id+"F3.wireOp",EDGE,"E1.sketch_text.stroke-1011"),sQuery(id+"F3.wireOp",EDGE,"E1.sketch_text.stroke-1012"),sQuery(id+"F3.wireOp",EDGE,"E1.sketch_text.stroke-1013"),sQuery(id+"F3.wireOp",EDGE,"E1.sketch_text.stroke-1014"),sQuery(id+"F3.wireOp",EDGE,"E1.sketch_text.stroke-1015"),sQuery(id+"F3.wireOp",EDGE,"E1.sketch_text.stroke-1016"),sQuery(id+"F3.wireOp",EDGE,"E1.sketch_text.stroke-1017"),sQuery(id+"F3.wireOp",EDGE,"E1.sketch_text.stroke-1018"),sQuery(id+"F3.wireOp",EDGE,"E1.sketch_text.stroke-1019"),sQuery(id+"F3.wireOp",EDGE,"E1.sketch_text.stroke-1020"),sQuery(id+"F3.wireOp",EDGE,"E1.sketch_text.stroke-1021"),sQuery(id+"F3.wireOp",EDGE,"E1.sketch_text.stroke-1022"),sQuery(id+"F3.wireOp",EDGE,"E1.sketch_text.stroke-1023"),sQuery(id+"F3.wireOp",EDGE,"E1.sketch_text.stroke-1024"),sQuery(id+"F3.wireOp",EDGE,"E1.sketch_text.stroke-1025"),sQuery(id+"F3.wireOp",EDGE,"E1.sketch_text.stroke-1026")])]});
            var Q68;
            Q68=makeQuery(id+"F4.opExtrude","SWEPT_BODY",BODY,{"disambiguationData":[OSD([sQuery(id+"F3.wireOp",EDGE,"E1.sketch_text.stroke-1027"),sQuery(id+"F3.wireOp",EDGE,"E1.sketch_text.stroke-1028"),sQuery(id+"F3.wireOp",EDGE,"E1.sketch_text.stroke-1029"),sQuery(id+"F3.wireOp",EDGE,"E1.sketch_text.stroke-1030"),sQuery(id+"F3.wireOp",EDGE,"E1.sketch_text.stroke-1031"),sQuery(id+"F3.wireOp",EDGE,"E1.sketch_text.stroke-1032")])]});
            var Q69;
            Q69=makeQuery(id+"F4.opExtrude","SWEPT_BODY",BODY,{"disambiguationData":[OSD([sQuery(id+"F3.wireOp",EDGE,"E1.sketch_text.stroke-1033"),sQuery(id+"F3.wireOp",EDGE,"E1.sketch_text.stroke-1034"),sQuery(id+"F3.wireOp",EDGE,"E1.sketch_text.stroke-1035"),sQuery(id+"F3.wireOp",EDGE,"E1.sketch_text.stroke-1036"),sQuery(id+"F3.wireOp",EDGE,"E1.sketch_text.stroke-1037"),sQuery(id+"F3.wireOp",EDGE,"E1.sketch_text.stroke-1038"),sQuery(id+"F3.wireOp",EDGE,"E1.sketch_text.stroke-1039"),sQuery(id+"F3.wireOp",EDGE,"E1.sketch_text.stroke-1040"),sQuery(id+"F3.wireOp",EDGE,"E1.sketch_text.stroke-1041"),sQuery(id+"F3.wireOp",EDGE,"E1.sketch_text.stroke-1042"),sQuery(id+"F3.wireOp",EDGE,"E1.sketch_text.stroke-1043"),sQuery(id+"F3.wireOp",EDGE,"E1.sketch_text.stroke-1044"),sQuery(id+"F3.wireOp",EDGE,"E1.sketch_text.stroke-1045"),sQuery(id+"F3.wireOp",EDGE,"E1.sketch_text.stroke-1046"),sQuery(id+"F3.wireOp",EDGE,"E1.sketch_text.stroke-1047"),sQuery(id+"F3.wireOp",EDGE,"E1.sketch_text.stroke-1048"),sQuery(id+"F3.wireOp",EDGE,"E1.sketch_text.stroke-1049"),sQuery(id+"F3.wireOp",EDGE,"E1.sketch_text.stroke-1050"),sQuery(id+"F3.wireOp",EDGE,"E1.sketch_text.stroke-1051"),sQuery(id+"F3.wireOp",EDGE,"E1.sketch_text.stroke-1052"),sQuery(id+"F3.wireOp",EDGE,"E1.sketch_text.stroke-1053"),sQuery(id+"F3.wireOp",EDGE,"E1.sketch_text.stroke-1054"),sQuery(id+"F3.wireOp",EDGE,"E1.sketch_text.stroke-1055"),sQuery(id+"F3.wireOp",EDGE,"E1.sketch_text.stroke-1056"),sQuery(id+"F3.wireOp",EDGE,"E1.sketch_text.stroke-1057"),sQuery(id+"F3.wireOp",EDGE,"E1.sketch_text.stroke-1058"),sQuery(id+"F3.wireOp",EDGE,"E1.sketch_text.stroke-1059")])]});
            var Q70;
            Q70=makeQuery(id+"F4.opExtrude","SWEPT_BODY",BODY,{"disambiguationData":[OSD([sQuery(id+"F3.wireOp",EDGE,"E1.sketch_text.stroke-1060"),sQuery(id+"F3.wireOp",EDGE,"E1.sketch_text.stroke-1061"),sQuery(id+"F3.wireOp",EDGE,"E1.sketch_text.stroke-1062"),sQuery(id+"F3.wireOp",EDGE,"E1.sketch_text.stroke-1063"),sQuery(id+"F3.wireOp",EDGE,"E1.sketch_text.stroke-1064"),sQuery(id+"F3.wireOp",EDGE,"E1.sketch_text.stroke-1065"),sQuery(id+"F3.wireOp",EDGE,"E1.sketch_text.stroke-1066")])]});
            var Q71;
            Q71=makeQuery(id+"F4.opExtrude","SWEPT_BODY",BODY,{"disambiguationData":[OSD([sQuery(id+"F3.wireOp",EDGE,"E1.sketch_text.stroke-1067"),sQuery(id+"F3.wireOp",EDGE,"E1.sketch_text.stroke-1068"),sQuery(id+"F3.wireOp",EDGE,"E1.sketch_text.stroke-1069"),sQuery(id+"F3.wireOp",EDGE,"E1.sketch_text.stroke-1070"),sQuery(id+"F3.wireOp",EDGE,"E1.sketch_text.stroke-1071"),sQuery(id+"F3.wireOp",EDGE,"E1.sketch_text.stroke-1072"),sQuery(id+"F3.wireOp",EDGE,"E1.sketch_text.stroke-1073")])]});
            var Q72;
            Q72=makeQuery(id+"F4.opExtrude","SWEPT_BODY",BODY,{"disambiguationData":[OSD([sQuery(id+"F3.wireOp",EDGE,"E1.sketch_text.stroke-1074"),sQuery(id+"F3.wireOp",EDGE,"E1.sketch_text.stroke-1075"),sQuery(id+"F3.wireOp",EDGE,"E1.sketch_text.stroke-1076"),sQuery(id+"F3.wireOp",EDGE,"E1.sketch_text.stroke-1077"),sQuery(id+"F3.wireOp",EDGE,"E1.sketch_text.stroke-1078"),sQuery(id+"F3.wireOp",EDGE,"E1.sketch_text.stroke-1079"),sQuery(id+"F3.wireOp",EDGE,"E1.sketch_text.stroke-1080"),sQuery(id+"F3.wireOp",EDGE,"E1.sketch_text.stroke-1081"),sQuery(id+"F3.wireOp",EDGE,"E1.sketch_text.stroke-1082"),sQuery(id+"F3.wireOp",EDGE,"E1.sketch_text.stroke-1083"),sQuery(id+"F3.wireOp",EDGE,"E1.sketch_text.stroke-1084"),sQuery(id+"F3.wireOp",EDGE,"E1.sketch_text.stroke-1085"),sQuery(id+"F3.wireOp",EDGE,"E1.sketch_text.stroke-1086"),sQuery(id+"F3.wireOp",EDGE,"E1.sketch_text.stroke-1087"),sQuery(id+"F3.wireOp",EDGE,"E1.sketch_text.stroke-1088"),sQuery(id+"F3.wireOp",EDGE,"E1.sketch_text.stroke-1089"),sQuery(id+"F3.wireOp",EDGE,"E1.sketch_text.stroke-1090"),sQuery(id+"F3.wireOp",EDGE,"E1.sketch_text.stroke-1091"),sQuery(id+"F3.wireOp",EDGE,"E1.sketch_text.stroke-1092"),sQuery(id+"F3.wireOp",EDGE,"E1.sketch_text.stroke-1093")])]});
            var Q73;
            Q73=makeQuery(id+"F4.opExtrude","SWEPT_BODY",BODY,{"disambiguationData":[OSD([sQuery(id+"F3.wireOp",EDGE,"E1.sketch_text.stroke-1094"),sQuery(id+"F3.wireOp",EDGE,"E1.sketch_text.stroke-1095"),sQuery(id+"F3.wireOp",EDGE,"E1.sketch_text.stroke-1096"),sQuery(id+"F3.wireOp",EDGE,"E1.sketch_text.stroke-1097"),sQuery(id+"F3.wireOp",EDGE,"E1.sketch_text.stroke-1098")])]});
            var Q74;
            Q74=makeQuery(id+"F4.opExtrude","SWEPT_BODY",BODY,{"disambiguationData":[OSD([sQuery(id+"F3.wireOp",EDGE,"E1.sketch_text.stroke-1099"),sQuery(id+"F3.wireOp",EDGE,"E1.sketch_text.stroke-1100"),sQuery(id+"F3.wireOp",EDGE,"E1.sketch_text.stroke-1101"),sQuery(id+"F3.wireOp",EDGE,"E1.sketch_text.stroke-1102"),sQuery(id+"F3.wireOp",EDGE,"E1.sketch_text.stroke-1103"),sQuery(id+"F3.wireOp",EDGE,"E1.sketch_text.stroke-1104"),sQuery(id+"F3.wireOp",EDGE,"E1.sketch_text.stroke-1105"),sQuery(id+"F3.wireOp",EDGE,"E1.sketch_text.stroke-1106"),sQuery(id+"F3.wireOp",EDGE,"E1.sketch_text.stroke-1107"),sQuery(id+"F3.wireOp",EDGE,"E1.sketch_text.stroke-1108"),sQuery(id+"F3.wireOp",EDGE,"E1.sketch_text.stroke-1109"),sQuery(id+"F3.wireOp",EDGE,"E1.sketch_text.stroke-1110"),sQuery(id+"F3.wireOp",EDGE,"E1.sketch_text.stroke-1111"),sQuery(id+"F3.wireOp",EDGE,"E1.sketch_text.stroke-1112"),sQuery(id+"F3.wireOp",EDGE,"E1.sketch_text.stroke-1113"),sQuery(id+"F3.wireOp",EDGE,"E1.sketch_text.stroke-1114"),sQuery(id+"F3.wireOp",EDGE,"E1.sketch_text.stroke-1115"),sQuery(id+"F3.wireOp",EDGE,"E1.sketch_text.stroke-1116"),sQuery(id+"F3.wireOp",EDGE,"E1.sketch_text.stroke-1117")])]});
            var Q75;
            Q75=makeQuery(id+"F4.opExtrude","SWEPT_BODY",BODY,{"disambiguationData":[OSD([sQuery(id+"F3.wireOp",EDGE,"E1.sketch_text.stroke-1118"),sQuery(id+"F3.wireOp",EDGE,"E1.sketch_text.stroke-1119"),sQuery(id+"F3.wireOp",EDGE,"E1.sketch_text.stroke-1120"),sQuery(id+"F3.wireOp",EDGE,"E1.sketch_text.stroke-1121"),sQuery(id+"F3.wireOp",EDGE,"E1.sketch_text.stroke-1122"),sQuery(id+"F3.wireOp",EDGE,"E1.sketch_text.stroke-1123"),sQuery(id+"F3.wireOp",EDGE,"E1.sketch_text.stroke-1124"),sQuery(id+"F3.wireOp",EDGE,"E1.sketch_text.stroke-1125"),sQuery(id+"F3.wireOp",EDGE,"E1.sketch_text.stroke-1126"),sQuery(id+"F3.wireOp",EDGE,"E1.sketch_text.stroke-1127"),sQuery(id+"F3.wireOp",EDGE,"E1.sketch_text.stroke-1128"),sQuery(id+"F3.wireOp",EDGE,"E1.sketch_text.stroke-1129"),sQuery(id+"F3.wireOp",EDGE,"E1.sketch_text.stroke-1130"),sQuery(id+"F3.wireOp",EDGE,"E1.sketch_text.stroke-1131"),sQuery(id+"F3.wireOp",EDGE,"E1.sketch_text.stroke-1132"),sQuery(id+"F3.wireOp",EDGE,"E1.sketch_text.stroke-1133"),sQuery(id+"F3.wireOp",EDGE,"E1.sketch_text.stroke-1134"),sQuery(id+"F3.wireOp",EDGE,"E1.sketch_text.stroke-1135"),sQuery(id+"F3.wireOp",EDGE,"E1.sketch_text.stroke-1136"),sQuery(id+"F3.wireOp",EDGE,"E1.sketch_text.stroke-1137"),sQuery(id+"F3.wireOp",EDGE,"E1.sketch_text.stroke-1138"),sQuery(id+"F3.wireOp",EDGE,"E1.sketch_text.stroke-1139"),sQuery(id+"F3.wireOp",EDGE,"E1.sketch_text.stroke-1140"),sQuery(id+"F3.wireOp",EDGE,"E1.sketch_text.stroke-1141"),sQuery(id+"F3.wireOp",EDGE,"E1.sketch_text.stroke-1142"),sQuery(id+"F3.wireOp",EDGE,"E1.sketch_text.stroke-1143"),sQuery(id+"F3.wireOp",EDGE,"E1.sketch_text.stroke-1144"),sQuery(id+"F3.wireOp",EDGE,"E1.sketch_text.stroke-1145"),sQuery(id+"F3.wireOp",EDGE,"E1.sketch_text.stroke-1146"),sQuery(id+"F3.wireOp",EDGE,"E1.sketch_text.stroke-1147"),sQuery(id+"F3.wireOp",EDGE,"E1.sketch_text.stroke-1148"),sQuery(id+"F3.wireOp",EDGE,"E1.sketch_text.stroke-1149"),sQuery(id+"F3.wireOp",EDGE,"E1.sketch_text.stroke-1150"),sQuery(id+"F3.wireOp",EDGE,"E1.sketch_text.stroke-1151"),sQuery(id+"F3.wireOp",EDGE,"E1.sketch_text.stroke-1152"),sQuery(id+"F3.wireOp",EDGE,"E1.sketch_text.stroke-1153")])]});
            var Q76;
            Q76=makeQuery(id+"F4.opExtrude","SWEPT_BODY",BODY,{"disambiguationData":[OSD([sQuery(id+"F3.wireOp",EDGE,"E1.sketch_text.stroke-1154"),sQuery(id+"F3.wireOp",EDGE,"E1.sketch_text.stroke-1155"),sQuery(id+"F3.wireOp",EDGE,"E1.sketch_text.stroke-1156"),sQuery(id+"F3.wireOp",EDGE,"E1.sketch_text.stroke-1157"),sQuery(id+"F3.wireOp",EDGE,"E1.sketch_text.stroke-1158"),sQuery(id+"F3.wireOp",EDGE,"E1.sketch_text.stroke-1159"),sQuery(id+"F3.wireOp",EDGE,"E1.sketch_text.stroke-1160")])]});
            var Q77;
            Q77=makeQuery(id+"F4.opExtrude","SWEPT_BODY",BODY,{"disambiguationData":[OSD([sQuery(id+"F3.wireOp",EDGE,"E1.sketch_text.stroke-1161"),sQuery(id+"F3.wireOp",EDGE,"E1.sketch_text.stroke-1162"),sQuery(id+"F3.wireOp",EDGE,"E1.sketch_text.stroke-1163"),sQuery(id+"F3.wireOp",EDGE,"E1.sketch_text.stroke-1164"),sQuery(id+"F3.wireOp",EDGE,"E1.sketch_text.stroke-1165"),sQuery(id+"F3.wireOp",EDGE,"E1.sketch_text.stroke-1166"),sQuery(id+"F3.wireOp",EDGE,"E1.sketch_text.stroke-1167")])]});
            var Q78;
            Q78=makeQuery(id+"F4.opExtrude","SWEPT_BODY",BODY,{"disambiguationData":[OSD([sQuery(id+"F3.wireOp",EDGE,"E1.sketch_text.stroke-1168"),sQuery(id+"F3.wireOp",EDGE,"E1.sketch_text.stroke-1169"),sQuery(id+"F3.wireOp",EDGE,"E1.sketch_text.stroke-1170"),sQuery(id+"F3.wireOp",EDGE,"E1.sketch_text.stroke-1171"),sQuery(id+"F3.wireOp",EDGE,"E1.sketch_text.stroke-1172"),sQuery(id+"F3.wireOp",EDGE,"E1.sketch_text.stroke-1173"),sQuery(id+"F3.wireOp",EDGE,"E1.sketch_text.stroke-1174"),sQuery(id+"F3.wireOp",EDGE,"E1.sketch_text.stroke-1175"),sQuery(id+"F3.wireOp",EDGE,"E1.sketch_text.stroke-1176"),sQuery(id+"F3.wireOp",EDGE,"E1.sketch_text.stroke-1177"),sQuery(id+"F3.wireOp",EDGE,"E1.sketch_text.stroke-1178"),sQuery(id+"F3.wireOp",EDGE,"E1.sketch_text.stroke-1179"),sQuery(id+"F3.wireOp",EDGE,"E1.sketch_text.stroke-1180"),sQuery(id+"F3.wireOp",EDGE,"E1.sketch_text.stroke-1181"),sQuery(id+"F3.wireOp",EDGE,"E1.sketch_text.stroke-1182"),sQuery(id+"F3.wireOp",EDGE,"E1.sketch_text.stroke-1183"),sQuery(id+"F3.wireOp",EDGE,"E1.sketch_text.stroke-1184"),sQuery(id+"F3.wireOp",EDGE,"E1.sketch_text.stroke-1185"),sQuery(id+"F3.wireOp",EDGE,"E1.sketch_text.stroke-1186"),sQuery(id+"F3.wireOp",EDGE,"E1.sketch_text.stroke-1187"),sQuery(id+"F3.wireOp",EDGE,"E1.sketch_text.stroke-1188"),sQuery(id+"F3.wireOp",EDGE,"E1.sketch_text.stroke-1189"),sQuery(id+"F3.wireOp",EDGE,"E1.sketch_text.stroke-1190"),sQuery(id+"F3.wireOp",EDGE,"E1.sketch_text.stroke-1191")])]});
            var Q79;
            Q79=makeQuery(id+"F4.opExtrude","SWEPT_BODY",BODY,{"disambiguationData":[OSD([sQuery(id+"F3.wireOp",EDGE,"E1.sketch_text.stroke-1192"),sQuery(id+"F3.wireOp",EDGE,"E1.sketch_text.stroke-1193"),sQuery(id+"F3.wireOp",EDGE,"E1.sketch_text.stroke-1194"),sQuery(id+"F3.wireOp",EDGE,"E1.sketch_text.stroke-1195"),sQuery(id+"F3.wireOp",EDGE,"E1.sketch_text.stroke-1196")])]});
            var Q80;
            Q80=makeQuery(id+"F4.opExtrude","SWEPT_BODY",BODY,{"disambiguationData":[OSD([sQuery(id+"F3.wireOp",EDGE,"E1.sketch_text.stroke-1197"),sQuery(id+"F3.wireOp",EDGE,"E1.sketch_text.stroke-1198"),sQuery(id+"F3.wireOp",EDGE,"E1.sketch_text.stroke-1199"),sQuery(id+"F3.wireOp",EDGE,"E1.sketch_text.stroke-1200"),sQuery(id+"F3.wireOp",EDGE,"E1.sketch_text.stroke-1201"),sQuery(id+"F3.wireOp",EDGE,"E1.sketch_text.stroke-1202"),sQuery(id+"F3.wireOp",EDGE,"E1.sketch_text.stroke-1203"),sQuery(id+"F3.wireOp",EDGE,"E1.sketch_text.stroke-1204"),sQuery(id+"F3.wireOp",EDGE,"E1.sketch_text.stroke-1205"),sQuery(id+"F3.wireOp",EDGE,"E1.sketch_text.stroke-1206"),sQuery(id+"F3.wireOp",EDGE,"E1.sketch_text.stroke-1207"),sQuery(id+"F3.wireOp",EDGE,"E1.sketch_text.stroke-1208"),sQuery(id+"F3.wireOp",EDGE,"E1.sketch_text.stroke-1209"),sQuery(id+"F3.wireOp",EDGE,"E1.sketch_text.stroke-1210"),sQuery(id+"F3.wireOp",EDGE,"E1.sketch_text.stroke-1211"),sQuery(id+"F3.wireOp",EDGE,"E1.sketch_text.stroke-1212"),sQuery(id+"F3.wireOp",EDGE,"E1.sketch_text.stroke-1213"),sQuery(id+"F3.wireOp",EDGE,"E1.sketch_text.stroke-1214"),sQuery(id+"F3.wireOp",EDGE,"E1.sketch_text.stroke-1215"),sQuery(id+"F3.wireOp",EDGE,"E1.sketch_text.stroke-1216"),sQuery(id+"F3.wireOp",EDGE,"E1.sketch_text.stroke-1217"),sQuery(id+"F3.wireOp",EDGE,"E1.sketch_text.stroke-1218"),sQuery(id+"F3.wireOp",EDGE,"E1.sketch_text.stroke-1219"),sQuery(id+"F3.wireOp",EDGE,"E1.sketch_text.stroke-1220")])]});
            var Q81;
            Q81=makeQuery(id+"F4.opExtrude","SWEPT_BODY",BODY,{"disambiguationData":[OSD([sQuery(id+"F3.wireOp",EDGE,"E1.sketch_text.stroke-1221"),sQuery(id+"F3.wireOp",EDGE,"E1.sketch_text.stroke-1222"),sQuery(id+"F3.wireOp",EDGE,"E1.sketch_text.stroke-1223"),sQuery(id+"F3.wireOp",EDGE,"E1.sketch_text.stroke-1224"),sQuery(id+"F3.wireOp",EDGE,"E1.sketch_text.stroke-1225"),sQuery(id+"F3.wireOp",EDGE,"E1.sketch_text.stroke-1226"),sQuery(id+"F3.wireOp",EDGE,"E1.sketch_text.stroke-1227"),sQuery(id+"F3.wireOp",EDGE,"E1.sketch_text.stroke-1228"),sQuery(id+"F3.wireOp",EDGE,"E1.sketch_text.stroke-1229"),sQuery(id+"F3.wireOp",EDGE,"E1.sketch_text.stroke-1230"),sQuery(id+"F3.wireOp",EDGE,"E1.sketch_text.stroke-1231"),sQuery(id+"F3.wireOp",EDGE,"E1.sketch_text.stroke-1232"),sQuery(id+"F3.wireOp",EDGE,"E1.sketch_text.stroke-1233"),sQuery(id+"F3.wireOp",EDGE,"E1.sketch_text.stroke-1234"),sQuery(id+"F3.wireOp",EDGE,"E1.sketch_text.stroke-1235"),sQuery(id+"F3.wireOp",EDGE,"E1.sketch_text.stroke-1236"),sQuery(id+"F3.wireOp",EDGE,"E1.sketch_text.stroke-1237"),sQuery(id+"F3.wireOp",EDGE,"E1.sketch_text.stroke-1238"),sQuery(id+"F3.wireOp",EDGE,"E1.sketch_text.stroke-1239"),sQuery(id+"F3.wireOp",EDGE,"E1.sketch_text.stroke-1240"),sQuery(id+"F3.wireOp",EDGE,"E1.sketch_text.stroke-1241"),sQuery(id+"F3.wireOp",EDGE,"E1.sketch_text.stroke-1242"),sQuery(id+"F3.wireOp",EDGE,"E1.sketch_text.stroke-1243"),sQuery(id+"F3.wireOp",EDGE,"E1.sketch_text.stroke-1244"),sQuery(id+"F3.wireOp",EDGE,"E1.sketch_text.stroke-1245"),sQuery(id+"F3.wireOp",EDGE,"E1.sketch_text.stroke-1246"),sQuery(id+"F3.wireOp",EDGE,"E1.sketch_text.stroke-1247"),sQuery(id+"F3.wireOp",EDGE,"E1.sketch_text.stroke-1248"),sQuery(id+"F3.wireOp",EDGE,"E1.sketch_text.stroke-1249"),sQuery(id+"F3.wireOp",EDGE,"E1.sketch_text.stroke-1250")])]});
            var Q82;
            Q82=makeQuery(id+"F4.opExtrude","SWEPT_BODY",BODY,{"disambiguationData":[OSD([sQuery(id+"F3.wireOp",EDGE,"E1.sketch_text.stroke-1251"),sQuery(id+"F3.wireOp",EDGE,"E1.sketch_text.stroke-1252"),sQuery(id+"F3.wireOp",EDGE,"E1.sketch_text.stroke-1253"),sQuery(id+"F3.wireOp",EDGE,"E1.sketch_text.stroke-1254"),sQuery(id+"F3.wireOp",EDGE,"E1.sketch_text.stroke-1255"),sQuery(id+"F3.wireOp",EDGE,"E1.sketch_text.stroke-1256"),sQuery(id+"F3.wireOp",EDGE,"E1.sketch_text.stroke-1257"),sQuery(id+"F3.wireOp",EDGE,"E1.sketch_text.stroke-1258"),sQuery(id+"F3.wireOp",EDGE,"E1.sketch_text.stroke-1259"),sQuery(id+"F3.wireOp",EDGE,"E1.sketch_text.stroke-1260"),sQuery(id+"F3.wireOp",EDGE,"E1.sketch_text.stroke-1261"),sQuery(id+"F3.wireOp",EDGE,"E1.sketch_text.stroke-1262"),sQuery(id+"F3.wireOp",EDGE,"E1.sketch_text.stroke-1263"),sQuery(id+"F3.wireOp",EDGE,"E1.sketch_text.stroke-1264")])]});
            var Q83;
            Q83=makeQuery(id+"F4.opExtrude","SWEPT_BODY",BODY,{"disambiguationData":[OSD([sQuery(id+"F3.wireOp",EDGE,"E1.sketch_text.stroke-1265"),sQuery(id+"F3.wireOp",EDGE,"E1.sketch_text.stroke-1266"),sQuery(id+"F3.wireOp",EDGE,"E1.sketch_text.stroke-1267"),sQuery(id+"F3.wireOp",EDGE,"E1.sketch_text.stroke-1268"),sQuery(id+"F3.wireOp",EDGE,"E1.sketch_text.stroke-1269"),sQuery(id+"F3.wireOp",EDGE,"E1.sketch_text.stroke-1270"),sQuery(id+"F3.wireOp",EDGE,"E1.sketch_text.stroke-1271"),sQuery(id+"F3.wireOp",EDGE,"E1.sketch_text.stroke-1272"),sQuery(id+"F3.wireOp",EDGE,"E1.sketch_text.stroke-1273"),sQuery(id+"F3.wireOp",EDGE,"E1.sketch_text.stroke-1274"),sQuery(id+"F3.wireOp",EDGE,"E1.sketch_text.stroke-1275"),sQuery(id+"F3.wireOp",EDGE,"E1.sketch_text.stroke-1276"),sQuery(id+"F3.wireOp",EDGE,"E1.sketch_text.stroke-1277"),sQuery(id+"F3.wireOp",EDGE,"E1.sketch_text.stroke-1278"),sQuery(id+"F3.wireOp",EDGE,"E1.sketch_text.stroke-1279"),sQuery(id+"F3.wireOp",EDGE,"E1.sketch_text.stroke-1280"),sQuery(id+"F3.wireOp",EDGE,"E1.sketch_text.stroke-1281"),sQuery(id+"F3.wireOp",EDGE,"E1.sketch_text.stroke-1282"),sQuery(id+"F3.wireOp",EDGE,"E1.sketch_text.stroke-1283"),sQuery(id+"F3.wireOp",EDGE,"E1.sketch_text.stroke-1284"),sQuery(id+"F3.wireOp",EDGE,"E1.sketch_text.stroke-1285"),sQuery(id+"F3.wireOp",EDGE,"E1.sketch_text.stroke-1286"),sQuery(id+"F3.wireOp",EDGE,"E1.sketch_text.stroke-1287"),sQuery(id+"F3.wireOp",EDGE,"E1.sketch_text.stroke-1288"),sQuery(id+"F3.wireOp",EDGE,"E1.sketch_text.stroke-1289"),sQuery(id+"F3.wireOp",EDGE,"E1.sketch_text.stroke-1290"),sQuery(id+"F3.wireOp",EDGE,"E1.sketch_text.stroke-1291"),sQuery(id+"F3.wireOp",EDGE,"E1.sketch_text.stroke-1292"),sQuery(id+"F3.wireOp",EDGE,"E1.sketch_text.stroke-1293"),sQuery(id+"F3.wireOp",EDGE,"E1.sketch_text.stroke-1294"),sQuery(id+"F3.wireOp",EDGE,"E1.sketch_text.stroke-1295"),sQuery(id+"F3.wireOp",EDGE,"E1.sketch_text.stroke-1296"),sQuery(id+"F3.wireOp",EDGE,"E1.sketch_text.stroke-1297")])]});
            var Q84;
            Q84=makeQuery(id+"F4.opExtrude","SWEPT_BODY",BODY,{"disambiguationData":[OSD([sQuery(id+"F3.wireOp",EDGE,"E1.sketch_text.stroke-1298"),sQuery(id+"F3.wireOp",EDGE,"E1.sketch_text.stroke-1299"),sQuery(id+"F3.wireOp",EDGE,"E1.sketch_text.stroke-1300"),sQuery(id+"F3.wireOp",EDGE,"E1.sketch_text.stroke-1301"),sQuery(id+"F3.wireOp",EDGE,"E1.sketch_text.stroke-1302"),sQuery(id+"F3.wireOp",EDGE,"E1.sketch_text.stroke-1303"),sQuery(id+"F3.wireOp",EDGE,"E1.sketch_text.stroke-1304"),sQuery(id+"F3.wireOp",EDGE,"E1.sketch_text.stroke-1305"),sQuery(id+"F3.wireOp",EDGE,"E1.sketch_text.stroke-1306"),sQuery(id+"F3.wireOp",EDGE,"E1.sketch_text.stroke-1307"),sQuery(id+"F3.wireOp",EDGE,"E1.sketch_text.stroke-1308"),sQuery(id+"F3.wireOp",EDGE,"E1.sketch_text.stroke-1309"),sQuery(id+"F3.wireOp",EDGE,"E1.sketch_text.stroke-1310"),sQuery(id+"F3.wireOp",EDGE,"E1.sketch_text.stroke-1311"),sQuery(id+"F3.wireOp",EDGE,"E1.sketch_text.stroke-1312"),sQuery(id+"F3.wireOp",EDGE,"E1.sketch_text.stroke-1313")])]});
            var Q85;
            Q85=makeQuery(id+"F4.opExtrude","SWEPT_BODY",BODY,{"disambiguationData":[OSD([sQuery(id+"F3.wireOp",EDGE,"E1.sketch_text.stroke-1314"),sQuery(id+"F3.wireOp",EDGE,"E1.sketch_text.stroke-1315"),sQuery(id+"F3.wireOp",EDGE,"E1.sketch_text.stroke-1316"),sQuery(id+"F3.wireOp",EDGE,"E1.sketch_text.stroke-1317"),sQuery(id+"F3.wireOp",EDGE,"E1.sketch_text.stroke-1318"),sQuery(id+"F3.wireOp",EDGE,"E1.sketch_text.stroke-1319"),sQuery(id+"F3.wireOp",EDGE,"E1.sketch_text.stroke-1320"),sQuery(id+"F3.wireOp",EDGE,"E1.sketch_text.stroke-1321"),sQuery(id+"F3.wireOp",EDGE,"E1.sketch_text.stroke-1322"),sQuery(id+"F3.wireOp",EDGE,"E1.sketch_text.stroke-1323"),sQuery(id+"F3.wireOp",EDGE,"E1.sketch_text.stroke-1324"),sQuery(id+"F3.wireOp",EDGE,"E1.sketch_text.stroke-1325"),sQuery(id+"F3.wireOp",EDGE,"E1.sketch_text.stroke-1326"),sQuery(id+"F3.wireOp",EDGE,"E1.sketch_text.stroke-1327"),sQuery(id+"F3.wireOp",EDGE,"E1.sketch_text.stroke-1328"),sQuery(id+"F3.wireOp",EDGE,"E1.sketch_text.stroke-1329"),sQuery(id+"F3.wireOp",EDGE,"E1.sketch_text.stroke-1330")])]});
            var Q86;
            Q86=makeQuery(id+"F4.opExtrude","SWEPT_BODY",BODY,{"disambiguationData":[OSD([sQuery(id+"F3.wireOp",EDGE,"E1.sketch_text.stroke-1331"),sQuery(id+"F3.wireOp",EDGE,"E1.sketch_text.stroke-1332"),sQuery(id+"F3.wireOp",EDGE,"E1.sketch_text.stroke-1333"),sQuery(id+"F3.wireOp",EDGE,"E1.sketch_text.stroke-1334"),sQuery(id+"F3.wireOp",EDGE,"E1.sketch_text.stroke-1335"),sQuery(id+"F3.wireOp",EDGE,"E1.sketch_text.stroke-1336"),sQuery(id+"F3.wireOp",EDGE,"E1.sketch_text.stroke-1337"),sQuery(id+"F3.wireOp",EDGE,"E1.sketch_text.stroke-1338"),sQuery(id+"F3.wireOp",EDGE,"E1.sketch_text.stroke-1339"),sQuery(id+"F3.wireOp",EDGE,"E1.sketch_text.stroke-1340"),sQuery(id+"F3.wireOp",EDGE,"E1.sketch_text.stroke-1341"),sQuery(id+"F3.wireOp",EDGE,"E1.sketch_text.stroke-1342"),sQuery(id+"F3.wireOp",EDGE,"E1.sketch_text.stroke-1343"),sQuery(id+"F3.wireOp",EDGE,"E1.sketch_text.stroke-1344"),sQuery(id+"F3.wireOp",EDGE,"E1.sketch_text.stroke-1345"),sQuery(id+"F3.wireOp",EDGE,"E1.sketch_text.stroke-1346")])]});
            var Q87;
            Q87=makeQuery(id+"F4.opExtrude","SWEPT_BODY",BODY,{"disambiguationData":[OSD([sQuery(id+"F3.wireOp",EDGE,"E1.sketch_text.stroke-1347"),sQuery(id+"F3.wireOp",EDGE,"E1.sketch_text.stroke-1348"),sQuery(id+"F3.wireOp",EDGE,"E1.sketch_text.stroke-1349"),sQuery(id+"F3.wireOp",EDGE,"E1.sketch_text.stroke-1350"),sQuery(id+"F3.wireOp",EDGE,"E1.sketch_text.stroke-1351"),sQuery(id+"F3.wireOp",EDGE,"E1.sketch_text.stroke-1352"),sQuery(id+"F3.wireOp",EDGE,"E1.sketch_text.stroke-1353"),sQuery(id+"F3.wireOp",EDGE,"E1.sketch_text.stroke-1354"),sQuery(id+"F3.wireOp",EDGE,"E1.sketch_text.stroke-1355"),sQuery(id+"F3.wireOp",EDGE,"E1.sketch_text.stroke-1356"),sQuery(id+"F3.wireOp",EDGE,"E1.sketch_text.stroke-1357"),sQuery(id+"F3.wireOp",EDGE,"E1.sketch_text.stroke-1358"),sQuery(id+"F3.wireOp",EDGE,"E1.sketch_text.stroke-1359"),sQuery(id+"F3.wireOp",EDGE,"E1.sketch_text.stroke-1360"),sQuery(id+"F3.wireOp",EDGE,"E1.sketch_text.stroke-1361"),sQuery(id+"F3.wireOp",EDGE,"E1.sketch_text.stroke-1362"),sQuery(id+"F3.wireOp",EDGE,"E1.sketch_text.stroke-1363")])]});
            var Q88;
            Q88=makeQuery(id+"F4.opExtrude","SWEPT_BODY",BODY,{"disambiguationData":[OSD([sQuery(id+"F3.wireOp",EDGE,"E1.sketch_text.stroke-1364"),sQuery(id+"F3.wireOp",EDGE,"E1.sketch_text.stroke-1365"),sQuery(id+"F3.wireOp",EDGE,"E1.sketch_text.stroke-1366"),sQuery(id+"F3.wireOp",EDGE,"E1.sketch_text.stroke-1367"),sQuery(id+"F3.wireOp",EDGE,"E1.sketch_text.stroke-1368"),sQuery(id+"F3.wireOp",EDGE,"E1.sketch_text.stroke-1369"),sQuery(id+"F3.wireOp",EDGE,"E1.sketch_text.stroke-1370"),sQuery(id+"F3.wireOp",EDGE,"E1.sketch_text.stroke-1371"),sQuery(id+"F3.wireOp",EDGE,"E1.sketch_text.stroke-1372"),sQuery(id+"F3.wireOp",EDGE,"E1.sketch_text.stroke-1373"),sQuery(id+"F3.wireOp",EDGE,"E1.sketch_text.stroke-1374"),sQuery(id+"F3.wireOp",EDGE,"E1.sketch_text.stroke-1375"),sQuery(id+"F3.wireOp",EDGE,"E1.sketch_text.stroke-1376"),sQuery(id+"F3.wireOp",EDGE,"E1.sketch_text.stroke-1377"),sQuery(id+"F3.wireOp",EDGE,"E1.sketch_text.stroke-1378"),sQuery(id+"F3.wireOp",EDGE,"E1.sketch_text.stroke-1379"),sQuery(id+"F3.wireOp",EDGE,"E1.sketch_text.stroke-1380"),sQuery(id+"F3.wireOp",EDGE,"E1.sketch_text.stroke-1381"),sQuery(id+"F3.wireOp",EDGE,"E1.sketch_text.stroke-1382"),sQuery(id+"F3.wireOp",EDGE,"E1.sketch_text.stroke-1383"),sQuery(id+"F3.wireOp",EDGE,"E1.sketch_text.stroke-1384"),sQuery(id+"F3.wireOp",EDGE,"E1.sketch_text.stroke-1385"),sQuery(id+"F3.wireOp",EDGE,"E1.sketch_text.stroke-1387"),sQuery(id+"F3.wireOp",EDGE,"E1.sketch_text.stroke-1388"),sQuery(id+"F3.wireOp",EDGE,"E1.sketch_text.stroke-1389"),sQuery(id+"F3.wireOp",EDGE,"E1.sketch_text.stroke-1390"),sQuery(id+"F3.wireOp",EDGE,"E1.sketch_text.stroke-1391"),sQuery(id+"F3.wireOp",EDGE,"E1.sketch_text.stroke-1392"),sQuery(id+"F3.wireOp",EDGE,"E1.sketch_text.stroke-1393"),sQuery(id+"F3.wireOp",EDGE,"E1.sketch_text.stroke-1394"),sQuery(id+"F3.wireOp",EDGE,"E1.sketch_text.stroke-1395"),sQuery(id+"F3.wireOp",EDGE,"E1.sketch_text.stroke-1396"),sQuery(id+"F3.wireOp",EDGE,"E1.sketch_text.stroke-1397"),sQuery(id+"F3.wireOp",EDGE,"E1.sketch_text.stroke-1398"),sQuery(id+"F3.wireOp",EDGE,"E1.sketch_text.stroke-1399"),sQuery(id+"F3.wireOp",EDGE,"E1.sketch_text.stroke-1400"),sQuery(id+"F3.wireOp",EDGE,"E1.sketch_text.stroke-1401"),sQuery(id+"F3.wireOp",EDGE,"E1.sketch_text.stroke-1402"),sQuery(id+"F3.wireOp",EDGE,"E1.sketch_text.stroke-1403"),sQuery(id+"F3.wireOp",EDGE,"E1.sketch_text.stroke-1404"),sQuery(id+"F3.wireOp",EDGE,"E1.sketch_text.stroke-1405"),sQuery(id+"F3.wireOp",EDGE,"E1.sketch_text.stroke-1406"),sQuery(id+"F3.wireOp",EDGE,"E1.sketch_text.stroke-1407"),sQuery(id+"F3.wireOp",EDGE,"E1.sketch_text.stroke-1408"),sQuery(id+"F3.wireOp",EDGE,"E1.sketch_text.stroke-1409")])]});
            var Q89;
            Q89=makeQuery(id+"F4.opExtrude","SWEPT_BODY",BODY,{"disambiguationData":[OSD([sQuery(id+"F3.wireOp",EDGE,"E1.sketch_text.stroke-1410"),sQuery(id+"F3.wireOp",EDGE,"E1.sketch_text.stroke-1411"),sQuery(id+"F3.wireOp",EDGE,"E1.sketch_text.stroke-1412"),sQuery(id+"F3.wireOp",EDGE,"E1.sketch_text.stroke-1413"),sQuery(id+"F3.wireOp",EDGE,"E1.sketch_text.stroke-1414"),sQuery(id+"F3.wireOp",EDGE,"E1.sketch_text.stroke-1415"),sQuery(id+"F3.wireOp",EDGE,"E1.sketch_text.stroke-1416")])]});
            var Q90;
            Q90=makeQuery(id+"F4.opExtrude","SWEPT_BODY",BODY,{"disambiguationData":[OSD([sQuery(id+"F3.wireOp",EDGE,"E1.sketch_text.stroke-1417"),sQuery(id+"F3.wireOp",EDGE,"E1.sketch_text.stroke-1418"),sQuery(id+"F3.wireOp",EDGE,"E1.sketch_text.stroke-1419"),sQuery(id+"F3.wireOp",EDGE,"E1.sketch_text.stroke-1420")])]});
            var Q91;
            Q91=makeQuery(id+"F4.opExtrude","SWEPT_BODY",BODY,{"disambiguationData":[OSD([sQuery(id+"F3.wireOp",EDGE,"E1.sketch_text.stroke-1421"),sQuery(id+"F3.wireOp",EDGE,"E1.sketch_text.stroke-1422"),sQuery(id+"F3.wireOp",EDGE,"E1.sketch_text.stroke-1423"),sQuery(id+"F3.wireOp",EDGE,"E1.sketch_text.stroke-1424"),sQuery(id+"F3.wireOp",EDGE,"E1.sketch_text.stroke-1425"),sQuery(id+"F3.wireOp",EDGE,"E1.sketch_text.stroke-1426"),sQuery(id+"F3.wireOp",EDGE,"E1.sketch_text.stroke-1427"),sQuery(id+"F3.wireOp",EDGE,"E1.sketch_text.stroke-1428"),sQuery(id+"F3.wireOp",EDGE,"E1.sketch_text.stroke-1429"),sQuery(id+"F3.wireOp",EDGE,"E1.sketch_text.stroke-1430"),sQuery(id+"F3.wireOp",EDGE,"E1.sketch_text.stroke-1431"),sQuery(id+"F3.wireOp",EDGE,"E1.sketch_text.stroke-1432"),sQuery(id+"F3.wireOp",EDGE,"E1.sketch_text.stroke-1433"),sQuery(id+"F3.wireOp",EDGE,"E1.sketch_text.stroke-1434"),sQuery(id+"F3.wireOp",EDGE,"E1.sketch_text.stroke-1435"),sQuery(id+"F3.wireOp",EDGE,"E1.sketch_text.stroke-1436"),sQuery(id+"F3.wireOp",EDGE,"E1.sketch_text.stroke-1437"),sQuery(id+"F3.wireOp",EDGE,"E1.sketch_text.stroke-1438"),sQuery(id+"F3.wireOp",EDGE,"E1.sketch_text.stroke-1439"),sQuery(id+"F3.wireOp",EDGE,"E1.sketch_text.stroke-1440"),sQuery(id+"F3.wireOp",EDGE,"E1.sketch_text.stroke-1441"),sQuery(id+"F3.wireOp",EDGE,"E1.sketch_text.stroke-1442"),sQuery(id+"F3.wireOp",EDGE,"E1.sketch_text.stroke-1443"),sQuery(id+"F3.wireOp",EDGE,"E1.sketch_text.stroke-1444"),sQuery(id+"F3.wireOp",EDGE,"E1.sketch_text.stroke-1445")])]});
            var Q92;
            Q92=makeQuery(id+"F4.opExtrude","SWEPT_BODY",BODY,{"disambiguationData":[OSD([sQuery(id+"F3.wireOp",EDGE,"E1.sketch_text.stroke-1446"),sQuery(id+"F3.wireOp",EDGE,"E1.sketch_text.stroke-1447"),sQuery(id+"F3.wireOp",EDGE,"E1.sketch_text.stroke-1448"),sQuery(id+"F3.wireOp",EDGE,"E1.sketch_text.stroke-1449"),sQuery(id+"F3.wireOp",EDGE,"E1.sketch_text.stroke-1450"),sQuery(id+"F3.wireOp",EDGE,"E1.sketch_text.stroke-1451"),sQuery(id+"F3.wireOp",EDGE,"E1.sketch_text.stroke-1452"),sQuery(id+"F3.wireOp",EDGE,"E1.sketch_text.stroke-1453"),sQuery(id+"F3.wireOp",EDGE,"E1.sketch_text.stroke-1454"),sQuery(id+"F3.wireOp",EDGE,"E1.sketch_text.stroke-1455"),sQuery(id+"F3.wireOp",EDGE,"E1.sketch_text.stroke-1456"),sQuery(id+"F3.wireOp",EDGE,"E1.sketch_text.stroke-1457"),sQuery(id+"F3.wireOp",EDGE,"E1.sketch_text.stroke-1458"),sQuery(id+"F3.wireOp",EDGE,"E1.sketch_text.stroke-1459"),sQuery(id+"F3.wireOp",EDGE,"E1.sketch_text.stroke-1460"),sQuery(id+"F3.wireOp",EDGE,"E1.sketch_text.stroke-1461"),sQuery(id+"F3.wireOp",EDGE,"E1.sketch_text.stroke-1462"),sQuery(id+"F3.wireOp",EDGE,"E1.sketch_text.stroke-1463")])]});
            var Q93;
            Q93=makeQuery(id+"F4.opExtrude","SWEPT_BODY",BODY,{"disambiguationData":[OSD([sQuery(id+"F3.wireOp",EDGE,"E1.sketch_text.stroke-1464"),sQuery(id+"F3.wireOp",EDGE,"E1.sketch_text.stroke-1465"),sQuery(id+"F3.wireOp",EDGE,"E1.sketch_text.stroke-1466"),sQuery(id+"F3.wireOp",EDGE,"E1.sketch_text.stroke-1467"),sQuery(id+"F3.wireOp",EDGE,"E1.sketch_text.stroke-1468"),sQuery(id+"F3.wireOp",EDGE,"E1.sketch_text.stroke-1469"),sQuery(id+"F3.wireOp",EDGE,"E1.sketch_text.stroke-1470"),sQuery(id+"F3.wireOp",EDGE,"E1.sketch_text.stroke-1471"),sQuery(id+"F3.wireOp",EDGE,"E1.sketch_text.stroke-1472"),sQuery(id+"F3.wireOp",EDGE,"E1.sketch_text.stroke-1473"),sQuery(id+"F3.wireOp",EDGE,"E1.sketch_text.stroke-1474"),sQuery(id+"F3.wireOp",EDGE,"E1.sketch_text.stroke-1475"),sQuery(id+"F3.wireOp",EDGE,"E1.sketch_text.stroke-1476"),sQuery(id+"F3.wireOp",EDGE,"E1.sketch_text.stroke-1477"),sQuery(id+"F3.wireOp",EDGE,"E1.sketch_text.stroke-1478"),sQuery(id+"F3.wireOp",EDGE,"E1.sketch_text.stroke-1479"),sQuery(id+"F3.wireOp",EDGE,"E1.sketch_text.stroke-1480"),sQuery(id+"F3.wireOp",EDGE,"E1.sketch_text.stroke-1481"),sQuery(id+"F3.wireOp",EDGE,"E1.sketch_text.stroke-1482")])]});
            var Q94;
            Q94=makeQuery(id+"F4.opExtrude","SWEPT_BODY",BODY,{"disambiguationData":[OSD([sQuery(id+"F3.wireOp",EDGE,"E1.sketch_text.stroke-1483"),sQuery(id+"F3.wireOp",EDGE,"E1.sketch_text.stroke-1484"),sQuery(id+"F3.wireOp",EDGE,"E1.sketch_text.stroke-1485"),sQuery(id+"F3.wireOp",EDGE,"E1.sketch_text.stroke-1486"),sQuery(id+"F3.wireOp",EDGE,"E1.sketch_text.stroke-1487"),sQuery(id+"F3.wireOp",EDGE,"E1.sketch_text.stroke-1488"),sQuery(id+"F3.wireOp",EDGE,"E1.sketch_text.stroke-1489"),sQuery(id+"F3.wireOp",EDGE,"E1.sketch_text.stroke-1490"),sQuery(id+"F3.wireOp",EDGE,"E1.sketch_text.stroke-1491"),sQuery(id+"F3.wireOp",EDGE,"E1.sketch_text.stroke-1492"),sQuery(id+"F3.wireOp",EDGE,"E1.sketch_text.stroke-1493"),sQuery(id+"F3.wireOp",EDGE,"E1.sketch_text.stroke-1494"),sQuery(id+"F3.wireOp",EDGE,"E1.sketch_text.stroke-1495"),sQuery(id+"F3.wireOp",EDGE,"E1.sketch_text.stroke-1496"),sQuery(id+"F3.wireOp",EDGE,"E1.sketch_text.stroke-1497"),sQuery(id+"F3.wireOp",EDGE,"E1.sketch_text.stroke-1498"),sQuery(id+"F3.wireOp",EDGE,"E1.sketch_text.stroke-1499"),sQuery(id+"F3.wireOp",EDGE,"E1.sketch_text.stroke-1500"),sQuery(id+"F3.wireOp",EDGE,"E1.sketch_text.stroke-1501"),sQuery(id+"F3.wireOp",EDGE,"E1.sketch_text.stroke-1502"),sQuery(id+"F3.wireOp",EDGE,"E1.sketch_text.stroke-1503"),sQuery(id+"F3.wireOp",EDGE,"E1.sketch_text.stroke-1504"),sQuery(id+"F3.wireOp",EDGE,"E1.sketch_text.stroke-1505"),sQuery(id+"F3.wireOp",EDGE,"E1.sketch_text.stroke-1506"),sQuery(id+"F3.wireOp",EDGE,"E1.sketch_text.stroke-1507"),sQuery(id+"F3.wireOp",EDGE,"E1.sketch_text.stroke-1508"),sQuery(id+"F3.wireOp",EDGE,"E1.sketch_text.stroke-1509"),sQuery(id+"F3.wireOp",EDGE,"E1.sketch_text.stroke-1510"),sQuery(id+"F3.wireOp",EDGE,"E1.sketch_text.stroke-1511"),sQuery(id+"F3.wireOp",EDGE,"E1.sketch_text.stroke-1512"),sQuery(id+"F3.wireOp",EDGE,"E1.sketch_text.stroke-1513"),sQuery(id+"F3.wireOp",EDGE,"E1.sketch_text.stroke-1514"),sQuery(id+"F3.wireOp",EDGE,"E1.sketch_text.stroke-1515"),sQuery(id+"F3.wireOp",EDGE,"E1.sketch_text.stroke-1516"),sQuery(id+"F3.wireOp",EDGE,"E1.sketch_text.stroke-1517"),sQuery(id+"F3.wireOp",EDGE,"E1.sketch_text.stroke-1518")])]});
            var Q95;
            Q95=makeQuery(id+"F4.opExtrude","SWEPT_BODY",BODY,{"disambiguationData":[OSD([sQuery(id+"F3.wireOp",EDGE,"E1.sketch_text.stroke-1519"),sQuery(id+"F3.wireOp",EDGE,"E1.sketch_text.stroke-1520"),sQuery(id+"F3.wireOp",EDGE,"E1.sketch_text.stroke-1521"),sQuery(id+"F3.wireOp",EDGE,"E1.sketch_text.stroke-1522"),sQuery(id+"F3.wireOp",EDGE,"E1.sketch_text.stroke-1523")])]});
            var Q96;
            Q96=makeQuery(id+"F4.opExtrude","SWEPT_BODY",BODY,{"disambiguationData":[OSD([sQuery(id+"F3.wireOp",EDGE,"E1.sketch_text.stroke-1524"),sQuery(id+"F3.wireOp",EDGE,"E1.sketch_text.stroke-1525"),sQuery(id+"F3.wireOp",EDGE,"E1.sketch_text.stroke-1526"),sQuery(id+"F3.wireOp",EDGE,"E1.sketch_text.stroke-1527"),sQuery(id+"F3.wireOp",EDGE,"E1.sketch_text.stroke-1528"),sQuery(id+"F3.wireOp",EDGE,"E1.sketch_text.stroke-1529"),sQuery(id+"F3.wireOp",EDGE,"E1.sketch_text.stroke-1530"),sQuery(id+"F3.wireOp",EDGE,"E1.sketch_text.stroke-1531"),sQuery(id+"F3.wireOp",EDGE,"E1.sketch_text.stroke-1532"),sQuery(id+"F3.wireOp",EDGE,"E1.sketch_text.stroke-1533"),sQuery(id+"F3.wireOp",EDGE,"E1.sketch_text.stroke-1534"),sQuery(id+"F3.wireOp",EDGE,"E1.sketch_text.stroke-1535"),sQuery(id+"F3.wireOp",EDGE,"E1.sketch_text.stroke-1536"),sQuery(id+"F3.wireOp",EDGE,"E1.sketch_text.stroke-1537"),sQuery(id+"F3.wireOp",EDGE,"E1.sketch_text.stroke-1538"),sQuery(id+"F3.wireOp",EDGE,"E1.sketch_text.stroke-1539"),sQuery(id+"F3.wireOp",EDGE,"E1.sketch_text.stroke-1540"),sQuery(id+"F3.wireOp",EDGE,"E1.sketch_text.stroke-1541"),sQuery(id+"F3.wireOp",EDGE,"E1.sketch_text.stroke-1542")])]});
            var Q97;
            Q97=makeQuery(id+"F4.opExtrude","SWEPT_BODY",BODY,{"disambiguationData":[OSD([sQuery(id+"F3.wireOp",EDGE,"E1.sketch_text.stroke-1543"),sQuery(id+"F3.wireOp",EDGE,"E1.sketch_text.stroke-1544"),sQuery(id+"F3.wireOp",EDGE,"E1.sketch_text.stroke-1545"),sQuery(id+"F3.wireOp",EDGE,"E1.sketch_text.stroke-1546"),sQuery(id+"F3.wireOp",EDGE,"E1.sketch_text.stroke-1547"),sQuery(id+"F3.wireOp",EDGE,"E1.sketch_text.stroke-1548"),sQuery(id+"F3.wireOp",EDGE,"E1.sketch_text.stroke-1549"),sQuery(id+"F3.wireOp",EDGE,"E1.sketch_text.stroke-1550"),sQuery(id+"F3.wireOp",EDGE,"E1.sketch_text.stroke-1551"),sQuery(id+"F3.wireOp",EDGE,"E1.sketch_text.stroke-1552"),sQuery(id+"F3.wireOp",EDGE,"E1.sketch_text.stroke-1553"),sQuery(id+"F3.wireOp",EDGE,"E1.sketch_text.stroke-1554"),sQuery(id+"F3.wireOp",EDGE,"E1.sketch_text.stroke-1555"),sQuery(id+"F3.wireOp",EDGE,"E1.sketch_text.stroke-1556"),sQuery(id+"F3.wireOp",EDGE,"E1.sketch_text.stroke-1557"),sQuery(id+"F3.wireOp",EDGE,"E1.sketch_text.stroke-1558"),sQuery(id+"F3.wireOp",EDGE,"E1.sketch_text.stroke-1559"),sQuery(id+"F3.wireOp",EDGE,"E1.sketch_text.stroke-1560"),sQuery(id+"F3.wireOp",EDGE,"E1.sketch_text.stroke-1561"),sQuery(id+"F3.wireOp",EDGE,"E1.sketch_text.stroke-1562"),sQuery(id+"F3.wireOp",EDGE,"E1.sketch_text.stroke-1563"),sQuery(id+"F3.wireOp",EDGE,"E1.sketch_text.stroke-1564"),sQuery(id+"F3.wireOp",EDGE,"E1.sketch_text.stroke-1565"),sQuery(id+"F3.wireOp",EDGE,"E1.sketch_text.stroke-1566"),sQuery(id+"F3.wireOp",EDGE,"E1.sketch_text.stroke-1567")])]});
            var Q98;
            Q98=makeQuery(id+"F4.opExtrude","SWEPT_BODY",BODY,{"disambiguationData":[OSD([sQuery(id+"F3.wireOp",EDGE,"E1.sketch_text.stroke-1568"),sQuery(id+"F3.wireOp",EDGE,"E1.sketch_text.stroke-1569"),sQuery(id+"F3.wireOp",EDGE,"E1.sketch_text.stroke-1570"),sQuery(id+"F3.wireOp",EDGE,"E1.sketch_text.stroke-1571"),sQuery(id+"F3.wireOp",EDGE,"E1.sketch_text.stroke-1572"),sQuery(id+"F3.wireOp",EDGE,"E1.sketch_text.stroke-1573"),sQuery(id+"F3.wireOp",EDGE,"E1.sketch_text.stroke-1574"),sQuery(id+"F3.wireOp",EDGE,"E1.sketch_text.stroke-1575"),sQuery(id+"F3.wireOp",EDGE,"E1.sketch_text.stroke-1576"),sQuery(id+"F3.wireOp",EDGE,"E1.sketch_text.stroke-1577"),sQuery(id+"F3.wireOp",EDGE,"E1.sketch_text.stroke-1578"),sQuery(id+"F3.wireOp",EDGE,"E1.sketch_text.stroke-1579"),sQuery(id+"F3.wireOp",EDGE,"E1.sketch_text.stroke-1580"),sQuery(id+"F3.wireOp",EDGE,"E1.sketch_text.stroke-1581"),sQuery(id+"F3.wireOp",EDGE,"E1.sketch_text.stroke-1582"),sQuery(id+"F3.wireOp",EDGE,"E1.sketch_text.stroke-1583"),sQuery(id+"F3.wireOp",EDGE,"E1.sketch_text.stroke-1584"),sQuery(id+"F3.wireOp",EDGE,"E1.sketch_text.stroke-1585"),sQuery(id+"F3.wireOp",EDGE,"E1.sketch_text.stroke-1586")])]});
            var Q99;
            Q99=makeQuery(id+"F4.opExtrude","SWEPT_BODY",BODY,{"disambiguationData":[OSD([sQuery(id+"F3.wireOp",EDGE,"E1.sketch_text.stroke-1587"),sQuery(id+"F3.wireOp",EDGE,"E1.sketch_text.stroke-1588"),sQuery(id+"F3.wireOp",EDGE,"E1.sketch_text.stroke-1589"),sQuery(id+"F3.wireOp",EDGE,"E1.sketch_text.stroke-1590"),sQuery(id+"F3.wireOp",EDGE,"E1.sketch_text.stroke-1591"),sQuery(id+"F3.wireOp",EDGE,"E1.sketch_text.stroke-1592"),sQuery(id+"F3.wireOp",EDGE,"E1.sketch_text.stroke-1593"),sQuery(id+"F3.wireOp",EDGE,"E1.sketch_text.stroke-1594"),sQuery(id+"F3.wireOp",EDGE,"E1.sketch_text.stroke-1595"),sQuery(id+"F3.wireOp",EDGE,"E1.sketch_text.stroke-1596"),sQuery(id+"F3.wireOp",EDGE,"E1.sketch_text.stroke-1597"),sQuery(id+"F3.wireOp",EDGE,"E1.sketch_text.stroke-1598"),sQuery(id+"F3.wireOp",EDGE,"E1.sketch_text.stroke-1599"),sQuery(id+"F3.wireOp",EDGE,"E1.sketch_text.stroke-1600"),sQuery(id+"F3.wireOp",EDGE,"E1.sketch_text.stroke-1601"),sQuery(id+"F3.wireOp",EDGE,"E1.sketch_text.stroke-1602"),sQuery(id+"F3.wireOp",EDGE,"E1.sketch_text.stroke-1603"),sQuery(id+"F3.wireOp",EDGE,"E1.sketch_text.stroke-1604"),sQuery(id+"F3.wireOp",EDGE,"E1.sketch_text.stroke-1605"),sQuery(id+"F3.wireOp",EDGE,"E1.sketch_text.stroke-1606"),sQuery(id+"F3.wireOp",EDGE,"E1.sketch_text.stroke-1607"),sQuery(id+"F3.wireOp",EDGE,"E1.sketch_text.stroke-1608"),sQuery(id+"F3.wireOp",EDGE,"E1.sketch_text.stroke-1609"),sQuery(id+"F3.wireOp",EDGE,"E1.sketch_text.stroke-1610"),sQuery(id+"F3.wireOp",EDGE,"E1.sketch_text.stroke-1611"),sQuery(id+"F3.wireOp",EDGE,"E1.sketch_text.stroke-1612"),sQuery(id+"F3.wireOp",EDGE,"E1.sketch_text.stroke-1613"),sQuery(id+"F3.wireOp",EDGE,"E1.sketch_text.stroke-1614"),sQuery(id+"F3.wireOp",EDGE,"E1.sketch_text.stroke-1615"),sQuery(id+"F3.wireOp",EDGE,"E1.sketch_text.stroke-1616"),sQuery(id+"F3.wireOp",EDGE,"E1.sketch_text.stroke-1617"),sQuery(id+"F3.wireOp",EDGE,"E1.sketch_text.stroke-1618"),sQuery(id+"F3.wireOp",EDGE,"E1.sketch_text.stroke-1619"),sQuery(id+"F3.wireOp",EDGE,"E1.sketch_text.stroke-1620"),sQuery(id+"F3.wireOp",EDGE,"E1.sketch_text.stroke-1621"),sQuery(id+"F3.wireOp",EDGE,"E1.sketch_text.stroke-1622")])]});
            var Q100;
            Q100=makeQuery(id+"F4.opExtrude","SWEPT_BODY",BODY,{"disambiguationData":[OSD([sQuery(id+"F3.wireOp",EDGE,"E1.sketch_text.stroke-1623"),sQuery(id+"F3.wireOp",EDGE,"E1.sketch_text.stroke-1624"),sQuery(id+"F3.wireOp",EDGE,"E1.sketch_text.stroke-1625"),sQuery(id+"F3.wireOp",EDGE,"E1.sketch_text.stroke-1626"),sQuery(id+"F3.wireOp",EDGE,"E1.sketch_text.stroke-1627"),sQuery(id+"F3.wireOp",EDGE,"E1.sketch_text.stroke-1628"),sQuery(id+"F3.wireOp",EDGE,"E1.sketch_text.stroke-1629"),sQuery(id+"F3.wireOp",EDGE,"E1.sketch_text.stroke-1630")])]});
            var Q101;
            Q101=makeQuery(id+"F4.opExtrude","SWEPT_BODY",BODY,{"disambiguationData":[OSD([sQuery(id+"F3.wireOp",EDGE,"E1.sketch_text.stroke-1631"),sQuery(id+"F3.wireOp",EDGE,"E1.sketch_text.stroke-1632"),sQuery(id+"F3.wireOp",EDGE,"E1.sketch_text.stroke-1633"),sQuery(id+"F3.wireOp",EDGE,"E1.sketch_text.stroke-1634"),sQuery(id+"F3.wireOp",EDGE,"E1.sketch_text.stroke-1635"),sQuery(id+"F3.wireOp",EDGE,"E1.sketch_text.stroke-1636"),sQuery(id+"F3.wireOp",EDGE,"E1.sketch_text.stroke-1637"),sQuery(id+"F3.wireOp",EDGE,"E1.sketch_text.stroke-1638"),sQuery(id+"F3.wireOp",EDGE,"E1.sketch_text.stroke-1639"),sQuery(id+"F3.wireOp",EDGE,"E1.sketch_text.stroke-1640"),sQuery(id+"F3.wireOp",EDGE,"E1.sketch_text.stroke-1641"),sQuery(id+"F3.wireOp",EDGE,"E1.sketch_text.stroke-1642"),sQuery(id+"F3.wireOp",EDGE,"E1.sketch_text.stroke-1643"),sQuery(id+"F3.wireOp",EDGE,"E1.sketch_text.stroke-1644"),sQuery(id+"F3.wireOp",EDGE,"E1.sketch_text.stroke-1645"),sQuery(id+"F3.wireOp",EDGE,"E1.sketch_text.stroke-1646"),sQuery(id+"F3.wireOp",EDGE,"E1.sketch_text.stroke-1647"),sQuery(id+"F3.wireOp",EDGE,"E1.sketch_text.stroke-1648")])]});
            var Q102;
            Q102=makeQuery(id+"F4.opExtrude","SWEPT_BODY",BODY,{"disambiguationData":[OSD([sQuery(id+"F3.wireOp",EDGE,"E1.sketch_text.stroke-1649"),sQuery(id+"F3.wireOp",EDGE,"E1.sketch_text.stroke-1650"),sQuery(id+"F3.wireOp",EDGE,"E1.sketch_text.stroke-1651"),sQuery(id+"F3.wireOp",EDGE,"E1.sketch_text.stroke-1652"),sQuery(id+"F3.wireOp",EDGE,"E1.sketch_text.stroke-1653"),sQuery(id+"F3.wireOp",EDGE,"E1.sketch_text.stroke-1654"),sQuery(id+"F3.wireOp",EDGE,"E1.sketch_text.stroke-1655"),sQuery(id+"F3.wireOp",EDGE,"E1.sketch_text.stroke-1656"),sQuery(id+"F3.wireOp",EDGE,"E1.sketch_text.stroke-1657"),sQuery(id+"F3.wireOp",EDGE,"E1.sketch_text.stroke-1658"),sQuery(id+"F3.wireOp",EDGE,"E1.sketch_text.stroke-1659"),sQuery(id+"F3.wireOp",EDGE,"E1.sketch_text.stroke-1660"),sQuery(id+"F3.wireOp",EDGE,"E1.sketch_text.stroke-1661"),sQuery(id+"F3.wireOp",EDGE,"E1.sketch_text.stroke-1662"),sQuery(id+"F3.wireOp",EDGE,"E1.sketch_text.stroke-1663")])]});
            var Q103;
            Q103=makeQuery(id+"F4.opExtrude","SWEPT_BODY",BODY,{"disambiguationData":[OSD([sQuery(id+"F3.wireOp",EDGE,"E1.sketch_text.stroke-1664"),sQuery(id+"F3.wireOp",EDGE,"E1.sketch_text.stroke-1665"),sQuery(id+"F3.wireOp",EDGE,"E1.sketch_text.stroke-1666"),sQuery(id+"F3.wireOp",EDGE,"E1.sketch_text.stroke-1667"),sQuery(id+"F3.wireOp",EDGE,"E1.sketch_text.stroke-1668"),sQuery(id+"F3.wireOp",EDGE,"E1.sketch_text.stroke-1669"),sQuery(id+"F3.wireOp",EDGE,"E1.sketch_text.stroke-1670"),sQuery(id+"F3.wireOp",EDGE,"E1.sketch_text.stroke-1671"),sQuery(id+"F3.wireOp",EDGE,"E1.sketch_text.stroke-1672"),sQuery(id+"F3.wireOp",EDGE,"E1.sketch_text.stroke-1673"),sQuery(id+"F3.wireOp",EDGE,"E1.sketch_text.stroke-1674"),sQuery(id+"F3.wireOp",EDGE,"E1.sketch_text.stroke-1675"),sQuery(id+"F3.wireOp",EDGE,"E1.sketch_text.stroke-1676")])]});
            var Q104;
            Q104=makeQuery(id+"F4.opExtrude","SWEPT_BODY",BODY,{"disambiguationData":[OSD([sQuery(id+"F3.wireOp",EDGE,"E1.sketch_text.stroke-1677"),sQuery(id+"F3.wireOp",EDGE,"E1.sketch_text.stroke-1678"),sQuery(id+"F3.wireOp",EDGE,"E1.sketch_text.stroke-1679"),sQuery(id+"F3.wireOp",EDGE,"E1.sketch_text.stroke-1680"),sQuery(id+"F3.wireOp",EDGE,"E1.sketch_text.stroke-1681"),sQuery(id+"F3.wireOp",EDGE,"E1.sketch_text.stroke-1682"),sQuery(id+"F3.wireOp",EDGE,"E1.sketch_text.stroke-1683"),sQuery(id+"F3.wireOp",EDGE,"E1.sketch_text.stroke-1684"),sQuery(id+"F3.wireOp",EDGE,"E1.sketch_text.stroke-1685"),sQuery(id+"F3.wireOp",EDGE,"E1.sketch_text.stroke-1686"),sQuery(id+"F3.wireOp",EDGE,"E1.sketch_text.stroke-1687"),sQuery(id+"F3.wireOp",EDGE,"E1.sketch_text.stroke-1688"),sQuery(id+"F3.wireOp",EDGE,"E1.sketch_text.stroke-1689"),sQuery(id+"F3.wireOp",EDGE,"E1.sketch_text.stroke-1690"),sQuery(id+"F3.wireOp",EDGE,"E1.sketch_text.stroke-1691"),sQuery(id+"F3.wireOp",EDGE,"E1.sketch_text.stroke-1692"),sQuery(id+"F3.wireOp",EDGE,"E1.sketch_text.stroke-1693"),sQuery(id+"F3.wireOp",EDGE,"E1.sketch_text.stroke-1694"),sQuery(id+"F3.wireOp",EDGE,"E1.sketch_text.stroke-1695"),sQuery(id+"F3.wireOp",EDGE,"E1.sketch_text.stroke-1696"),sQuery(id+"F3.wireOp",EDGE,"E1.sketch_text.stroke-1697"),sQuery(id+"F3.wireOp",EDGE,"E1.sketch_text.stroke-1698"),sQuery(id+"F3.wireOp",EDGE,"E1.sketch_text.stroke-1699"),sQuery(id+"F3.wireOp",EDGE,"E1.sketch_text.stroke-1700")])]});
            var Q105;
            Q105=makeQuery(id+"F4.opExtrude","SWEPT_BODY",BODY,{"disambiguationData":[OSD([sQuery(id+"F3.wireOp",EDGE,"E1.sketch_text.stroke-1701"),sQuery(id+"F3.wireOp",EDGE,"E1.sketch_text.stroke-1702"),sQuery(id+"F3.wireOp",EDGE,"E1.sketch_text.stroke-1703"),sQuery(id+"F3.wireOp",EDGE,"E1.sketch_text.stroke-1704"),sQuery(id+"F3.wireOp",EDGE,"E1.sketch_text.stroke-1705"),sQuery(id+"F3.wireOp",EDGE,"E1.sketch_text.stroke-1706"),sQuery(id+"F3.wireOp",EDGE,"E1.sketch_text.stroke-1707"),sQuery(id+"F3.wireOp",EDGE,"E1.sketch_text.stroke-1708"),sQuery(id+"F3.wireOp",EDGE,"E1.sketch_text.stroke-1709"),sQuery(id+"F3.wireOp",EDGE,"E1.sketch_text.stroke-1710"),sQuery(id+"F3.wireOp",EDGE,"E1.sketch_text.stroke-1711"),sQuery(id+"F3.wireOp",EDGE,"E1.sketch_text.stroke-1712"),sQuery(id+"F3.wireOp",EDGE,"E1.sketch_text.stroke-1713"),sQuery(id+"F3.wireOp",EDGE,"E1.sketch_text.stroke-1714"),sQuery(id+"F3.wireOp",EDGE,"E1.sketch_text.stroke-1715"),sQuery(id+"F3.wireOp",EDGE,"E1.sketch_text.stroke-1716")])]});
            var Q106;
            Q106=makeQuery(id+"F4.opExtrude","SWEPT_BODY",BODY,{"disambiguationData":[OSD([sQuery(id+"F3.wireOp",EDGE,"E1.sketch_text.stroke-1717"),sQuery(id+"F3.wireOp",EDGE,"E1.sketch_text.stroke-1718"),sQuery(id+"F3.wireOp",EDGE,"E1.sketch_text.stroke-1719"),sQuery(id+"F3.wireOp",EDGE,"E1.sketch_text.stroke-1720"),sQuery(id+"F3.wireOp",EDGE,"E1.sketch_text.stroke-1721"),sQuery(id+"F3.wireOp",EDGE,"E1.sketch_text.stroke-1722"),sQuery(id+"F3.wireOp",EDGE,"E1.sketch_text.stroke-1723"),sQuery(id+"F3.wireOp",EDGE,"E1.sketch_text.stroke-1724"),sQuery(id+"F3.wireOp",EDGE,"E1.sketch_text.stroke-1725"),sQuery(id+"F3.wireOp",EDGE,"E1.sketch_text.stroke-1726"),sQuery(id+"F3.wireOp",EDGE,"E1.sketch_text.stroke-1727"),sQuery(id+"F3.wireOp",EDGE,"E1.sketch_text.stroke-1728"),sQuery(id+"F3.wireOp",EDGE,"E1.sketch_text.stroke-1729"),sQuery(id+"F3.wireOp",EDGE,"E1.sketch_text.stroke-1730"),sQuery(id+"F3.wireOp",EDGE,"E1.sketch_text.stroke-1731"),sQuery(id+"F3.wireOp",EDGE,"E1.sketch_text.stroke-1732")])]});
            var Q107;
            Q107=makeQuery(id+"F4.opExtrude","SWEPT_BODY",BODY,{"disambiguationData":[OSD([sQuery(id+"F3.wireOp",EDGE,"E1.sketch_text.stroke-1733"),sQuery(id+"F3.wireOp",EDGE,"E1.sketch_text.stroke-1734"),sQuery(id+"F3.wireOp",EDGE,"E1.sketch_text.stroke-1735"),sQuery(id+"F3.wireOp",EDGE,"E1.sketch_text.stroke-1736"),sQuery(id+"F3.wireOp",EDGE,"E1.sketch_text.stroke-1737"),sQuery(id+"F3.wireOp",EDGE,"E1.sketch_text.stroke-1738"),sQuery(id+"F3.wireOp",EDGE,"E1.sketch_text.stroke-1739")])]});
            var Q108;
            Q108=makeQuery(id+"F4.opExtrude","SWEPT_BODY",BODY,{"disambiguationData":[OSD([sQuery(id+"F3.wireOp",EDGE,"E1.sketch_text.stroke-1740"),sQuery(id+"F3.wireOp",EDGE,"E1.sketch_text.stroke-1741"),sQuery(id+"F3.wireOp",EDGE,"E1.sketch_text.stroke-1742"),sQuery(id+"F3.wireOp",EDGE,"E1.sketch_text.stroke-1743"),sQuery(id+"F3.wireOp",EDGE,"E1.sketch_text.stroke-1744"),sQuery(id+"F3.wireOp",EDGE,"E1.sketch_text.stroke-1745"),sQuery(id+"F3.wireOp",EDGE,"E1.sketch_text.stroke-1746")])]});
            var Q109;
            Q109=makeQuery(id+"F4.opExtrude","SWEPT_BODY",BODY,{"disambiguationData":[OSD([sQuery(id+"F3.wireOp",EDGE,"E1.sketch_text.stroke-1747"),sQuery(id+"F3.wireOp",EDGE,"E1.sketch_text.stroke-1748"),sQuery(id+"F3.wireOp",EDGE,"E1.sketch_text.stroke-1749"),sQuery(id+"F3.wireOp",EDGE,"E1.sketch_text.stroke-1750"),sQuery(id+"F3.wireOp",EDGE,"E1.sketch_text.stroke-1751"),sQuery(id+"F3.wireOp",EDGE,"E1.sketch_text.stroke-1752"),sQuery(id+"F3.wireOp",EDGE,"E1.sketch_text.stroke-1753"),sQuery(id+"F3.wireOp",EDGE,"E1.sketch_text.stroke-1754"),sQuery(id+"F3.wireOp",EDGE,"E1.sketch_text.stroke-1755"),sQuery(id+"F3.wireOp",EDGE,"E1.sketch_text.stroke-1756"),sQuery(id+"F3.wireOp",EDGE,"E1.sketch_text.stroke-1757"),sQuery(id+"F3.wireOp",EDGE,"E1.sketch_text.stroke-1758"),sQuery(id+"F3.wireOp",EDGE,"E1.sketch_text.stroke-1759"),sQuery(id+"F3.wireOp",EDGE,"E1.sketch_text.stroke-1760"),sQuery(id+"F3.wireOp",EDGE,"E1.sketch_text.stroke-1761"),sQuery(id+"F3.wireOp",EDGE,"E1.sketch_text.stroke-1762"),sQuery(id+"F3.wireOp",EDGE,"E1.sketch_text.stroke-1763"),sQuery(id+"F3.wireOp",EDGE,"E1.sketch_text.stroke-1764"),sQuery(id+"F3.wireOp",EDGE,"E1.sketch_text.stroke-1765"),sQuery(id+"F3.wireOp",EDGE,"E1.sketch_text.stroke-1766"),sQuery(id+"F3.wireOp",EDGE,"E1.sketch_text.stroke-1767"),sQuery(id+"F3.wireOp",EDGE,"E1.sketch_text.stroke-1768"),sQuery(id+"F3.wireOp",EDGE,"E1.sketch_text.stroke-1769"),sQuery(id+"F3.wireOp",EDGE,"E1.sketch_text.stroke-1770"),sQuery(id+"F3.wireOp",EDGE,"E1.sketch_text.stroke-1771"),sQuery(id+"F3.wireOp",EDGE,"E1.sketch_text.stroke-1772")])]});
            var Q110;
            Q110=makeQuery(id+"F4.opExtrude","SWEPT_BODY",BODY,{"disambiguationData":[OSD([sQuery(id+"F3.wireOp",EDGE,"E1.sketch_text.stroke-1773"),sQuery(id+"F3.wireOp",EDGE,"E1.sketch_text.stroke-1774"),sQuery(id+"F3.wireOp",EDGE,"E1.sketch_text.stroke-1775"),sQuery(id+"F3.wireOp",EDGE,"E1.sketch_text.stroke-1776"),sQuery(id+"F3.wireOp",EDGE,"E1.sketch_text.stroke-1777"),sQuery(id+"F3.wireOp",EDGE,"E1.sketch_text.stroke-1778"),sQuery(id+"F3.wireOp",EDGE,"E1.sketch_text.stroke-1779"),sQuery(id+"F3.wireOp",EDGE,"E1.sketch_text.stroke-1780"),sQuery(id+"F3.wireOp",EDGE,"E1.sketch_text.stroke-1781"),sQuery(id+"F3.wireOp",EDGE,"E1.sketch_text.stroke-1782"),sQuery(id+"F3.wireOp",EDGE,"E1.sketch_text.stroke-1783"),sQuery(id+"F3.wireOp",EDGE,"E1.sketch_text.stroke-1784"),sQuery(id+"F3.wireOp",EDGE,"E1.sketch_text.stroke-1785"),sQuery(id+"F3.wireOp",EDGE,"E1.sketch_text.stroke-1786"),sQuery(id+"F3.wireOp",EDGE,"E1.sketch_text.stroke-1787"),sQuery(id+"F3.wireOp",EDGE,"E1.sketch_text.stroke-1788"),sQuery(id+"F3.wireOp",EDGE,"E1.sketch_text.stroke-1789")])]});
            var Q111;
            Q111=makeQuery(id+"F4.opExtrude","SWEPT_BODY",BODY,{"disambiguationData":[OSD([sQuery(id+"F3.wireOp",EDGE,"E1.sketch_text.stroke-1790"),sQuery(id+"F3.wireOp",EDGE,"E1.sketch_text.stroke-1791"),sQuery(id+"F3.wireOp",EDGE,"E1.sketch_text.stroke-1792"),sQuery(id+"F3.wireOp",EDGE,"E1.sketch_text.stroke-1793")])]});
            var Q112;
            Q112=makeQuery(id+"F4.opExtrude","SWEPT_BODY",BODY,{"disambiguationData":[OSD([sQuery(id+"F3.wireOp",EDGE,"E1.sketch_text.stroke-1794"),sQuery(id+"F3.wireOp",EDGE,"E1.sketch_text.stroke-1795"),sQuery(id+"F3.wireOp",EDGE,"E1.sketch_text.stroke-1796"),sQuery(id+"F3.wireOp",EDGE,"E1.sketch_text.stroke-1797"),sQuery(id+"F3.wireOp",EDGE,"E1.sketch_text.stroke-1798"),sQuery(id+"F3.wireOp",EDGE,"E1.sketch_text.stroke-1799"),sQuery(id+"F3.wireOp",EDGE,"E1.sketch_text.stroke-1800"),sQuery(id+"F3.wireOp",EDGE,"E1.sketch_text.stroke-1801")])]});
            var Q113;
            Q113=makeQuery(id+"F4.opExtrude","SWEPT_BODY",BODY,{"disambiguationData":[OSD([sQuery(id+"F3.wireOp",EDGE,"E1.sketch_text.stroke-1802"),sQuery(id+"F3.wireOp",EDGE,"E1.sketch_text.stroke-1803"),sQuery(id+"F3.wireOp",EDGE,"E1.sketch_text.stroke-1804"),sQuery(id+"F3.wireOp",EDGE,"E1.sketch_text.stroke-1805"),sQuery(id+"F3.wireOp",EDGE,"E1.sketch_text.stroke-1806"),sQuery(id+"F3.wireOp",EDGE,"E1.sketch_text.stroke-1807"),sQuery(id+"F3.wireOp",EDGE,"E1.sketch_text.stroke-1808"),sQuery(id+"F3.wireOp",EDGE,"E1.sketch_text.stroke-1809"),sQuery(id+"F3.wireOp",EDGE,"E1.sketch_text.stroke-1810"),sQuery(id+"F3.wireOp",EDGE,"E1.sketch_text.stroke-1811"),sQuery(id+"F3.wireOp",EDGE,"E1.sketch_text.stroke-1812"),sQuery(id+"F3.wireOp",EDGE,"E1.sketch_text.stroke-1813"),sQuery(id+"F3.wireOp",EDGE,"E1.sketch_text.stroke-1814"),sQuery(id+"F3.wireOp",EDGE,"E1.sketch_text.stroke-1815"),sQuery(id+"F3.wireOp",EDGE,"E1.sketch_text.stroke-1816"),sQuery(id+"F3.wireOp",EDGE,"E1.sketch_text.stroke-1817"),sQuery(id+"F3.wireOp",EDGE,"E1.sketch_text.stroke-1818"),sQuery(id+"F3.wireOp",EDGE,"E1.sketch_text.stroke-1819"),sQuery(id+"F3.wireOp",EDGE,"E1.sketch_text.stroke-1820")])]});
            var Q114;
            Q114=makeQuery(id+"F4.opExtrude","SWEPT_BODY",BODY,{"disambiguationData":[OSD([sQuery(id+"F3.wireOp",EDGE,"E1.sketch_text.stroke-1821"),sQuery(id+"F3.wireOp",EDGE,"E1.sketch_text.stroke-1822"),sQuery(id+"F3.wireOp",EDGE,"E1.sketch_text.stroke-1823"),sQuery(id+"F3.wireOp",EDGE,"E1.sketch_text.stroke-1824"),sQuery(id+"F3.wireOp",EDGE,"E1.sketch_text.stroke-1825"),sQuery(id+"F3.wireOp",EDGE,"E1.sketch_text.stroke-1826"),sQuery(id+"F3.wireOp",EDGE,"E1.sketch_text.stroke-1827"),sQuery(id+"F3.wireOp",EDGE,"E1.sketch_text.stroke-1828"),sQuery(id+"F3.wireOp",EDGE,"E1.sketch_text.stroke-1829"),sQuery(id+"F3.wireOp",EDGE,"E1.sketch_text.stroke-1830"),sQuery(id+"F3.wireOp",EDGE,"E1.sketch_text.stroke-1831"),sQuery(id+"F3.wireOp",EDGE,"E1.sketch_text.stroke-1832"),sQuery(id+"F3.wireOp",EDGE,"E1.sketch_text.stroke-1833"),sQuery(id+"F3.wireOp",EDGE,"E1.sketch_text.stroke-1834"),sQuery(id+"F3.wireOp",EDGE,"E1.sketch_text.stroke-1835"),sQuery(id+"F3.wireOp",EDGE,"E1.sketch_text.stroke-1836"),sQuery(id+"F3.wireOp",EDGE,"E1.sketch_text.stroke-1837"),sQuery(id+"F3.wireOp",EDGE,"E1.sketch_text.stroke-1838"),sQuery(id+"F3.wireOp",EDGE,"E1.sketch_text.stroke-1839"),sQuery(id+"F3.wireOp",EDGE,"E1.sketch_text.stroke-1840"),sQuery(id+"F3.wireOp",EDGE,"E1.sketch_text.stroke-1841"),sQuery(id+"F3.wireOp",EDGE,"E1.sketch_text.stroke-1842"),sQuery(id+"F3.wireOp",EDGE,"E1.sketch_text.stroke-1843"),sQuery(id+"F3.wireOp",EDGE,"E1.sketch_text.stroke-1844"),sQuery(id+"F3.wireOp",EDGE,"E1.sketch_text.stroke-1845"),sQuery(id+"F3.wireOp",EDGE,"E1.sketch_text.stroke-1846"),sQuery(id+"F3.wireOp",EDGE,"E1.sketch_text.stroke-1847"),sQuery(id+"F3.wireOp",EDGE,"E1.sketch_text.stroke-1848"),sQuery(id+"F3.wireOp",EDGE,"E1.sketch_text.stroke-1849"),sQuery(id+"F3.wireOp",EDGE,"E1.sketch_text.stroke-1850"),sQuery(id+"F3.wireOp",EDGE,"E1.sketch_text.stroke-1851"),sQuery(id+"F3.wireOp",EDGE,"E1.sketch_text.stroke-1852"),sQuery(id+"F3.wireOp",EDGE,"E1.sketch_text.stroke-1853"),sQuery(id+"F3.wireOp",EDGE,"E1.sketch_text.stroke-1854"),sQuery(id+"F3.wireOp",EDGE,"E1.sketch_text.stroke-1855"),sQuery(id+"F3.wireOp",EDGE,"E1.sketch_text.stroke-1856")])]});
            var Q115;
            Q115=makeQuery(id+"F1.opExtrude","CAP_VERTEX",VERTEX,{"disambiguationData":[OSD([sQuery(id+"F0.wireOp",EDGE,"E0.bottom"),sQuery(id+"F0.wireOp",EDGE,"E0.right")])],"isStart":false});
            transform(context, id + "F5", {"entities" : qUnion([Q0, Q1, Q2, Q3, Q4, Q5, Q6, Q7, Q8, Q9, Q10, Q11, Q12, Q13, Q14, Q15, Q16, Q17, Q18, Q19, Q20, Q21, Q22, Q23, Q24, Q25, Q26, Q27, Q28, Q29, Q30, Q31, Q32, Q33, Q34, Q35, Q36, Q37, Q38, Q39, Q40, Q41, Q42, Q43, Q44, Q45, Q46, Q47, Q48, Q49, Q50, Q51, Q52, Q53, Q54, Q55, Q56, Q57, Q58, Q59, Q60, Q61, Q62, Q63, Q64, Q65, Q66, Q67, Q68, Q69, Q70, Q71, Q72, Q73, Q74, Q75, Q76, Q77, Q78, Q79, Q80, Q81, Q82, Q83, Q84, Q85, Q86, Q87, Q88, Q89, Q90, Q91, Q92, Q93, Q94, Q95, Q96, Q97, Q98, Q99, Q100, Q101, Q102, Q103, Q104, Q105, Q106, Q107, Q108, Q109, Q110, Q111, Q112, Q113, Q114]), "transformType" : TransformType.SCALE_UNIFORMLY, "scale" : .13, "scalePoint" : qUnion([Q115]), "makeCopy" : false});
        }
        {
            var Q0;
            Q0=makeQuery(id+"F4.opExtrude","SWEPT_BODY",BODY,{"disambiguationData":[OSD([sQuery(id+"F3.wireOp",EDGE,"E1.sketch_text.stroke-0"),sQuery(id+"F3.wireOp",EDGE,"E1.sketch_text.stroke-1"),sQuery(id+"F3.wireOp",EDGE,"E1.sketch_text.stroke-2"),sQuery(id+"F3.wireOp",EDGE,"E1.sketch_text.stroke-3"),sQuery(id+"F3.wireOp",EDGE,"E1.sketch_text.stroke-4"),sQuery(id+"F3.wireOp",EDGE,"E1.sketch_text.stroke-5"),sQuery(id+"F3.wireOp",EDGE,"E1.sketch_text.stroke-6"),sQuery(id+"F3.wireOp",EDGE,"E1.sketch_text.stroke-7")])]});
            var Q1;
            Q1=makeQuery(id+"F1.opExtrude","CAP_VERTEX",VERTEX,{"disambiguationData":[OSD([sQuery(id+"F0.wireOp",EDGE,"E0.bottom"),sQuery(id+"F0.wireOp",EDGE,"E0.right")])],"isStart":false});
            transform(context, id + "F6", {"entities" : qUnion([Q0]), "transformType" : TransformType.SCALE_UNIFORMLY, "scale" : .13, "scalePoint" : qUnion([Q1]), "makeCopy" : false});
        }
    });
